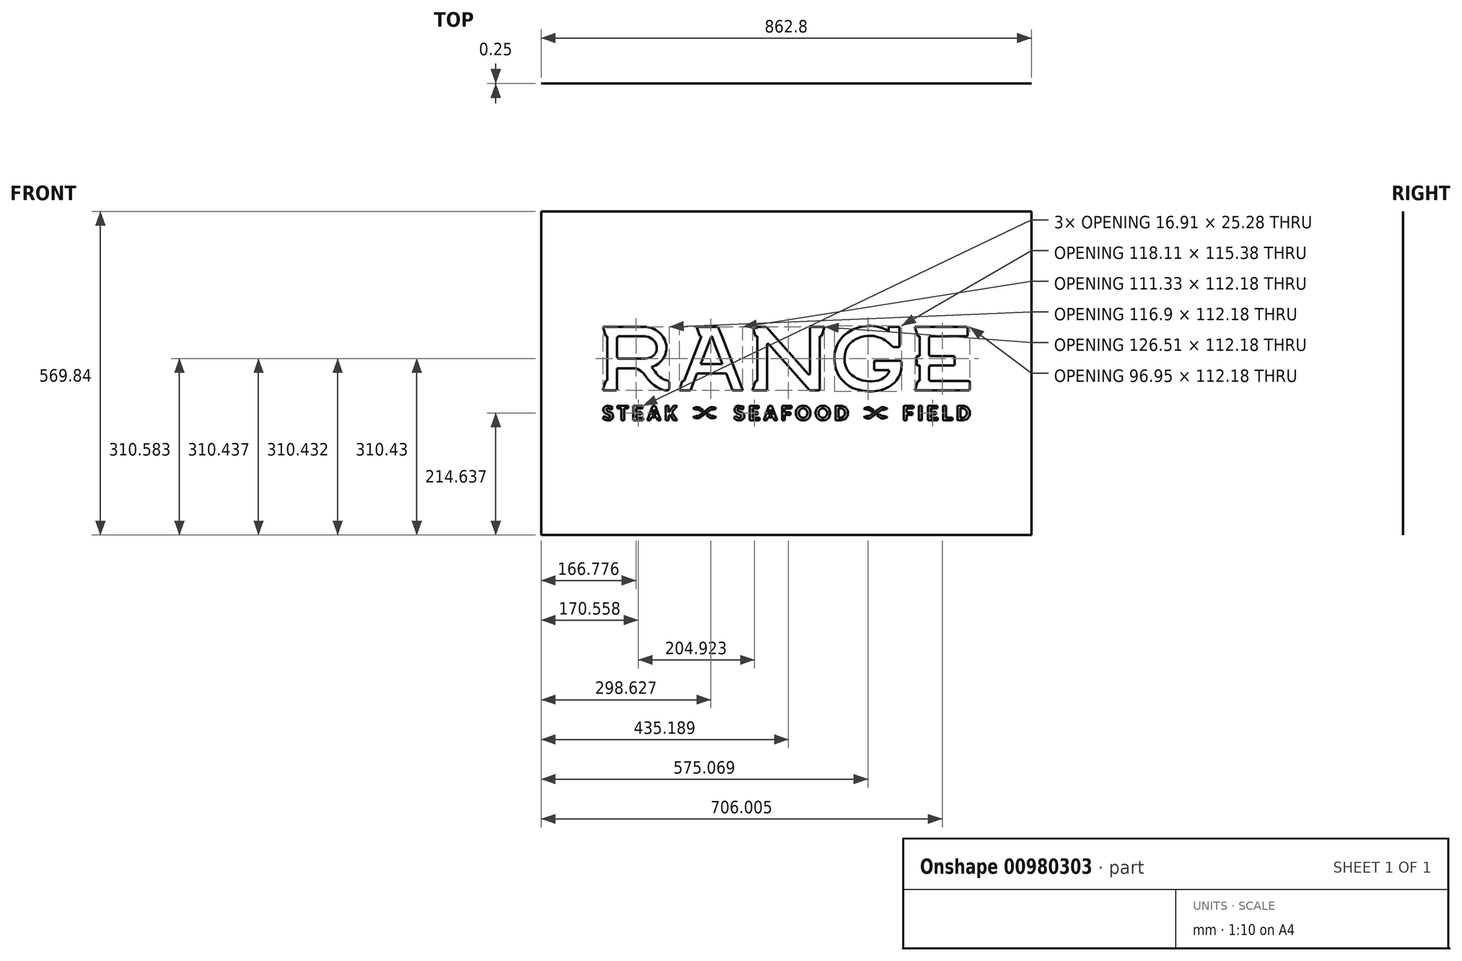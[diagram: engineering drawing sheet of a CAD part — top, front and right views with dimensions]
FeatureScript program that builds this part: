
annotation { "Feature Type Name" : "Feature", "Feature Type Description" : "" }
export const myFeature = defineFeature(function(context is Context, id is Id, definition is map)
    precondition{}
    {
        {
            var Q0;
            Q0=qCreatedBy(makeId("Front.planeOp"),FACE);
            var sketch = newSketch(context, id + "F0", { "sketchPlane" : qUnion([Q0])});
            skLineSegment(sketch, "E0", {"start": v(323.08, -28.35) * mm, "end": v(323.08, -28.56) * mm});
            skLineSegment(sketch, "E1", {"start": v(323.08, -28.56) * mm, "end": v(322.9, -29.21) * mm});
            skLineSegment(sketch, "E2", {"start": v(322.9, -29.21) * mm, "end": v(322.43, -29.93) * mm});
            skLineSegment(sketch, "E3", {"start": v(322.43, -29.93) * mm, "end": v(321.72, -30.4) * mm});
            skLineSegment(sketch, "E4", {"start": v(321.72, -30.4) * mm, "end": v(321.06, -30.58) * mm});
            skLineSegment(sketch, "E5", {"start": v(321.06, -30.58) * mm, "end": v(320.85, -30.58) * mm});
            skLineSegment(sketch, "E6", {"start": v(320.85, -30.58) * mm, "end": v(226.94, -30.58) * mm});
            skLineSegment(sketch, "E7", {"start": v(226.94, -30.58) * mm, "end": v(226.77, -30.58) * mm});
            skLineSegment(sketch, "E8", {"start": v(226.77, -30.58) * mm, "end": v(226.3, -30.29) * mm});
            skLineSegment(sketch, "E9", {"start": v(226.3, -30.29) * mm, "end": v(226.27, -30.23) * mm});
            skLineSegment(sketch, "E10", {"start": v(226.27, -30.23) * mm, "end": v(226.23, -30.18) * mm});
            skLineSegment(sketch, "E11", {"start": v(226.23, -30.18) * mm, "end": v(226.13, -29.55) * mm});
            skLineSegment(sketch, "E12", {"start": v(226.13, -29.55) * mm, "end": v(226.15, -29.49) * mm});
            skLineSegment(sketch, "E13", {"start": v(226.15, -29.49) * mm, "end": v(231.45, -13.62) * mm});
            skLineSegment(sketch, "E14", {"start": v(231.45, -13.62) * mm, "end": v(234.45, -13.62) * mm});
            skLineSegment(sketch, "E15", {"start": v(234.45, -13.62) * mm, "end": v(234.45, 13.2) * mm});
            skLineSegment(sketch, "E16", {"start": v(234.45, 13.2) * mm, "end": v(229.63, 13.2) * mm});
            skLineSegment(sketch, "E17", {"start": v(229.63, 13.2) * mm, "end": v(229.63, 30.16) * mm});
            skLineSegment(sketch, "E18", {"start": v(229.63, 30.16) * mm, "end": v(234.45, 30.16) * mm});
            skLineSegment(sketch, "E19", {"start": v(234.45, 30.16) * mm, "end": v(234.45, 64.64) * mm});
            skLineSegment(sketch, "E20", {"start": v(234.45, 64.64) * mm, "end": v(231.45, 64.64) * mm});
            skLineSegment(sketch, "E21", {"start": v(231.45, 64.64) * mm, "end": v(226.2, 80.39) * mm});
            skLineSegment(sketch, "E22", {"start": v(226.2, 80.39) * mm, "end": v(226.17, 80.46) * mm});
            skLineSegment(sketch, "E23", {"start": v(226.17, 80.46) * mm, "end": v(226.28, 81.16) * mm});
            skLineSegment(sketch, "E24", {"start": v(226.28, 81.16) * mm, "end": v(226.32, 81.22) * mm});
            skLineSegment(sketch, "E25", {"start": v(226.32, 81.22) * mm, "end": v(226.37, 81.28) * mm});
            skLineSegment(sketch, "E26", {"start": v(226.37, 81.28) * mm, "end": v(226.65, 81.5) * mm});
            skLineSegment(sketch, "E27", {"start": v(226.65, 81.5) * mm, "end": v(226.96, 81.6) * mm});
            skLineSegment(sketch, "E28", {"start": v(226.96, 81.6) * mm, "end": v(227.07, 81.6) * mm});
            skLineSegment(sketch, "E29", {"start": v(227.07, 81.6) * mm, "end": v(316.93, 81.6) * mm});
            skLineSegment(sketch, "E30", {"start": v(316.93, 81.6) * mm, "end": v(317.15, 81.6) * mm});
            skLineSegment(sketch, "E31", {"start": v(317.15, 81.6) * mm, "end": v(317.8, 81.43) * mm});
            skLineSegment(sketch, "E32", {"start": v(317.8, 81.43) * mm, "end": v(318.5, 80.95) * mm});
            skLineSegment(sketch, "E33", {"start": v(318.5, 80.95) * mm, "end": v(318.98, 80.24) * mm});
            skLineSegment(sketch, "E34", {"start": v(318.98, 80.24) * mm, "end": v(319.16, 79.59) * mm});
            skLineSegment(sketch, "E35", {"start": v(319.16, 79.59) * mm, "end": v(319.16, 79.37) * mm});
            skLineSegment(sketch, "E36", {"start": v(319.16, 79.37) * mm, "end": v(319.16, 66.87) * mm});
            skLineSegment(sketch, "E37", {"start": v(319.16, 66.87) * mm, "end": v(319.16, 66.66) * mm});
            skLineSegment(sketch, "E38", {"start": v(319.16, 66.66) * mm, "end": v(318.98, 66) * mm});
            skLineSegment(sketch, "E39", {"start": v(318.98, 66) * mm, "end": v(318.5, 65.3) * mm});
            skLineSegment(sketch, "E40", {"start": v(318.5, 65.3) * mm, "end": v(317.8, 64.82) * mm});
            skLineSegment(sketch, "E41", {"start": v(317.8, 64.82) * mm, "end": v(317.15, 64.64) * mm});
            skLineSegment(sketch, "E42", {"start": v(317.15, 64.64) * mm, "end": v(316.93, 64.64) * mm});
            skLineSegment(sketch, "E43", {"start": v(316.93, 64.64) * mm, "end": v(253.65, 64.64) * mm});
            skLineSegment(sketch, "E44", {"start": v(253.65, 64.64) * mm, "end": v(253.43, 64.64) * mm});
            skLineSegment(sketch, "E45", {"start": v(253.43, 64.64) * mm, "end": v(252.78, 64.47) * mm});
            skLineSegment(sketch, "E46", {"start": v(252.78, 64.47) * mm, "end": v(252.06, 63.98) * mm});
            skLineSegment(sketch, "E47", {"start": v(252.06, 63.98) * mm, "end": v(251.58, 63.27) * mm});
            skLineSegment(sketch, "E48", {"start": v(251.58, 63.27) * mm, "end": v(251.4, 62.61) * mm});
            skLineSegment(sketch, "E49", {"start": v(251.4, 62.61) * mm, "end": v(251.4, 62.4) * mm});
            skLineSegment(sketch, "E50", {"start": v(251.4, 62.4) * mm, "end": v(251.4, 32.4) * mm});
            skLineSegment(sketch, "E51", {"start": v(251.4, 32.4) * mm, "end": v(251.4, 32.2) * mm});
            skLineSegment(sketch, "E52", {"start": v(251.4, 32.2) * mm, "end": v(251.58, 31.54) * mm});
            skLineSegment(sketch, "E53", {"start": v(251.58, 31.54) * mm, "end": v(252.06, 30.82) * mm});
            skLineSegment(sketch, "E54", {"start": v(252.06, 30.82) * mm, "end": v(252.78, 30.34) * mm});
            skLineSegment(sketch, "E55", {"start": v(252.78, 30.34) * mm, "end": v(253.43, 30.16) * mm});
            skLineSegment(sketch, "E56", {"start": v(253.43, 30.16) * mm, "end": v(253.65, 30.16) * mm});
            skLineSegment(sketch, "E57", {"start": v(253.65, 30.16) * mm, "end": v(294.13, 30.16) * mm});
            skLineSegment(sketch, "E58", {"start": v(294.13, 30.16) * mm, "end": v(294.35, 30.16) * mm});
            skLineSegment(sketch, "E59", {"start": v(294.35, 30.16) * mm, "end": v(295, 29.99) * mm});
            skLineSegment(sketch, "E60", {"start": v(295, 29.99) * mm, "end": v(295.7, 29.51) * mm});
            skLineSegment(sketch, "E61", {"start": v(295.7, 29.51) * mm, "end": v(296.18, 28.8) * mm});
            skLineSegment(sketch, "E62", {"start": v(296.18, 28.8) * mm, "end": v(296.36, 28.15) * mm});
            skLineSegment(sketch, "E63", {"start": v(296.36, 28.15) * mm, "end": v(296.36, 27.93) * mm});
            skLineSegment(sketch, "E64", {"start": v(296.36, 27.93) * mm, "end": v(296.36, 15.43) * mm});
            skLineSegment(sketch, "E65", {"start": v(296.36, 15.43) * mm, "end": v(296.36, 15.22) * mm});
            skLineSegment(sketch, "E66", {"start": v(296.36, 15.22) * mm, "end": v(296.18, 14.57) * mm});
            skLineSegment(sketch, "E67", {"start": v(296.18, 14.57) * mm, "end": v(295.7, 13.86) * mm});
            skLineSegment(sketch, "E68", {"start": v(295.7, 13.86) * mm, "end": v(295, 13.38) * mm});
            skLineSegment(sketch, "E69", {"start": v(295, 13.38) * mm, "end": v(294.35, 13.2) * mm});
            skLineSegment(sketch, "E70", {"start": v(294.35, 13.2) * mm, "end": v(294.13, 13.2) * mm});
            skLineSegment(sketch, "E71", {"start": v(294.13, 13.2) * mm, "end": v(253.65, 13.2) * mm});
            skLineSegment(sketch, "E72", {"start": v(253.65, 13.2) * mm, "end": v(253.43, 13.2) * mm});
            skLineSegment(sketch, "E73", {"start": v(253.43, 13.2) * mm, "end": v(252.78, 13.03) * mm});
            skLineSegment(sketch, "E74", {"start": v(252.78, 13.03) * mm, "end": v(252.06, 12.55) * mm});
            skLineSegment(sketch, "E75", {"start": v(252.06, 12.55) * mm, "end": v(251.58, 11.83) * mm});
            skLineSegment(sketch, "E76", {"start": v(251.58, 11.83) * mm, "end": v(251.4, 11.17) * mm});
            skLineSegment(sketch, "E77", {"start": v(251.4, 11.17) * mm, "end": v(251.4, 10.96) * mm});
            skLineSegment(sketch, "E78", {"start": v(251.4, 10.96) * mm, "end": v(251.4, -11.37) * mm});
            skLineSegment(sketch, "E79", {"start": v(251.4, -11.37) * mm, "end": v(251.4, -11.59) * mm});
            skLineSegment(sketch, "E80", {"start": v(251.4, -11.59) * mm, "end": v(251.58, -12.25) * mm});
            skLineSegment(sketch, "E81", {"start": v(251.58, -12.25) * mm, "end": v(252.06, -12.96) * mm});
            skLineSegment(sketch, "E82", {"start": v(252.06, -12.96) * mm, "end": v(252.78, -13.44) * mm});
            skLineSegment(sketch, "E83", {"start": v(252.78, -13.44) * mm, "end": v(253.43, -13.62) * mm});
            skLineSegment(sketch, "E84", {"start": v(253.43, -13.62) * mm, "end": v(253.65, -13.62) * mm});
            skLineSegment(sketch, "E85", {"start": v(253.65, -13.62) * mm, "end": v(320.85, -13.62) * mm});
            skLineSegment(sketch, "E86", {"start": v(320.85, -13.62) * mm, "end": v(321.06, -13.62) * mm});
            skLineSegment(sketch, "E87", {"start": v(321.06, -13.62) * mm, "end": v(321.72, -13.8) * mm});
            skLineSegment(sketch, "E88", {"start": v(321.72, -13.8) * mm, "end": v(322.43, -14.27) * mm});
            skLineSegment(sketch, "E89", {"start": v(322.43, -14.27) * mm, "end": v(322.9, -14.98) * mm});
            skLineSegment(sketch, "E90", {"start": v(322.9, -14.98) * mm, "end": v(323.08, -15.63) * mm});
            skLineSegment(sketch, "E91", {"start": v(323.08, -15.63) * mm, "end": v(323.08, -15.85) * mm});
            skLineSegment(sketch, "E92", {"start": v(323.08, -15.85) * mm, "end": v(323.08, -28.35) * mm});
            skLineSegment(sketch, "E93", {"start": v(310.05, -82.92) * mm, "end": v(301.57, -82.92) * mm});
            skLineSegment(sketch, "E94", {"start": v(301.57, -82.92) * mm, "end": v(301.57, -57.64) * mm});
            skLineSegment(sketch, "E95", {"start": v(301.57, -57.64) * mm, "end": v(309.94, -57.64) * mm});
            skLineSegment(sketch, "E96", {"start": v(309.94, -57.64) * mm, "end": v(310.66, -57.64) * mm});
            skLineSegment(sketch, "E97", {"start": v(310.66, -57.64) * mm, "end": v(312.8, -57.88) * mm});
            skLineSegment(sketch, "E98", {"start": v(312.8, -57.88) * mm, "end": v(315.37, -58.57) * mm});
            skLineSegment(sketch, "E99", {"start": v(315.37, -58.57) * mm, "end": v(317.62, -59.68) * mm});
            skLineSegment(sketch, "E100", {"start": v(317.62, -59.68) * mm, "end": v(319.52, -61.18) * mm});
            skLineSegment(sketch, "E101", {"start": v(319.52, -61.18) * mm, "end": v(321.03, -63.02) * mm});
            skLineSegment(sketch, "E102", {"start": v(321.03, -63.02) * mm, "end": v(322.15, -65.18) * mm});
            skLineSegment(sketch, "E103", {"start": v(322.15, -65.18) * mm, "end": v(322.84, -67.63) * mm});
            skLineSegment(sketch, "E104", {"start": v(322.84, -67.63) * mm, "end": v(323.08, -69.64) * mm});
            skLineSegment(sketch, "E105", {"start": v(323.08, -69.64) * mm, "end": v(323.08, -70.32) * mm});
            skLineSegment(sketch, "E106", {"start": v(323.08, -70.32) * mm, "end": v(323.08, -70.99) * mm});
            skLineSegment(sketch, "E107", {"start": v(323.08, -70.99) * mm, "end": v(322.85, -73) * mm});
            skLineSegment(sketch, "E108", {"start": v(322.85, -73) * mm, "end": v(322.18, -75.43) * mm});
            skLineSegment(sketch, "E109", {"start": v(322.18, -75.43) * mm, "end": v(321.1, -77.58) * mm});
            skLineSegment(sketch, "E110", {"start": v(321.1, -77.58) * mm, "end": v(319.6, -79.41) * mm});
            skLineSegment(sketch, "E111", {"start": v(319.6, -79.41) * mm, "end": v(317.73, -80.9) * mm});
            skLineSegment(sketch, "E112", {"start": v(317.73, -80.9) * mm, "end": v(315.5, -82) * mm});
            skLineSegment(sketch, "E113", {"start": v(315.5, -82) * mm, "end": v(312.94, -82.69) * mm});
            skLineSegment(sketch, "E114", {"start": v(312.94, -82.69) * mm, "end": v(310.77, -82.92) * mm});
            skLineSegment(sketch, "E115", {"start": v(310.77, -82.92) * mm, "end": v(310.05, -82.92) * mm});
            skLineSegment(sketch, "E116", {"start": v(292.36, -82.92) * mm, "end": v(276.09, -82.92) * mm});
            skLineSegment(sketch, "E117", {"start": v(276.09, -82.92) * mm, "end": v(276.09, -57.64) * mm});
            skLineSegment(sketch, "E118", {"start": v(276.09, -57.64) * mm, "end": v(281.11, -57.64) * mm});
            skLineSegment(sketch, "E119", {"start": v(281.11, -57.64) * mm, "end": v(281.11, -78.47) * mm});
            skLineSegment(sketch, "E120", {"start": v(281.11, -78.47) * mm, "end": v(292.36, -78.47) * mm});
            skLineSegment(sketch, "E121", {"start": v(292.36, -78.47) * mm, "end": v(292.36, -82.92) * mm});
            skLineSegment(sketch, "E122", {"start": v(266.3, -82.92) * mm, "end": v(249.4, -82.92) * mm});
            skLineSegment(sketch, "E123", {"start": v(249.4, -82.92) * mm, "end": v(249.4, -57.64) * mm});
            skLineSegment(sketch, "E124", {"start": v(249.4, -57.64) * mm, "end": v(265.56, -57.64) * mm});
            skLineSegment(sketch, "E125", {"start": v(265.56, -57.64) * mm, "end": v(265.56, -62.13) * mm});
            skLineSegment(sketch, "E126", {"start": v(265.56, -62.13) * mm, "end": v(254.3, -62.13) * mm});
            skLineSegment(sketch, "E127", {"start": v(254.3, -62.13) * mm, "end": v(254.3, -68.18) * mm});
            skLineSegment(sketch, "E128", {"start": v(254.3, -68.18) * mm, "end": v(263.31, -68.18) * mm});
            skLineSegment(sketch, "E129", {"start": v(263.31, -68.18) * mm, "end": v(263.31, -72.6) * mm});
            skLineSegment(sketch, "E130", {"start": v(263.31, -72.6) * mm, "end": v(254.3, -72.6) * mm});
            skLineSegment(sketch, "E131", {"start": v(254.3, -72.6) * mm, "end": v(254.3, -78.47) * mm});
            skLineSegment(sketch, "E132", {"start": v(254.3, -78.47) * mm, "end": v(266.3, -78.47) * mm});
            skLineSegment(sketch, "E133", {"start": v(266.3, -78.47) * mm, "end": v(266.3, -82.92) * mm});
            skLineSegment(sketch, "E134", {"start": v(238.33, -82.92) * mm, "end": v(233.3, -82.92) * mm});
            skLineSegment(sketch, "E135", {"start": v(233.3, -82.92) * mm, "end": v(233.3, -57.64) * mm});
            skLineSegment(sketch, "E136", {"start": v(233.3, -57.64) * mm, "end": v(238.33, -57.64) * mm});
            skLineSegment(sketch, "E137", {"start": v(238.33, -57.64) * mm, "end": v(238.33, -82.92) * mm});
            skLineSegment(sketch, "E138", {"start": v(223.63, -62.13) * mm, "end": v(211.81, -62.13) * mm});
            skLineSegment(sketch, "E139", {"start": v(211.81, -62.13) * mm, "end": v(211.81, -68.86) * mm});
            skLineSegment(sketch, "E140", {"start": v(211.81, -68.86) * mm, "end": v(221.67, -68.86) * mm});
            skLineSegment(sketch, "E141", {"start": v(221.67, -68.86) * mm, "end": v(221.67, -73.34) * mm});
            skLineSegment(sketch, "E142", {"start": v(221.67, -73.34) * mm, "end": v(211.81, -73.34) * mm});
            skLineSegment(sketch, "E143", {"start": v(211.81, -73.34) * mm, "end": v(211.81, -82.92) * mm});
            skLineSegment(sketch, "E144", {"start": v(211.81, -82.92) * mm, "end": v(206.86, -82.92) * mm});
            skLineSegment(sketch, "E145", {"start": v(206.86, -82.92) * mm, "end": v(206.86, -57.64) * mm});
            skLineSegment(sketch, "E146", {"start": v(206.86, -57.64) * mm, "end": v(223.63, -57.64) * mm});
            skLineSegment(sketch, "E147", {"start": v(223.63, -57.64) * mm, "end": v(223.63, -62.13) * mm});
            skLineSegment(sketch, "E148", {"start": v(202.19, 7.48) * mm, "end": v(202.03, 6.34) * mm});
            skLineSegment(sketch, "E149", {"start": v(202.03, 6.34) * mm, "end": v(200.76, 0.89) * mm});
            skLineSegment(sketch, "E150", {"start": v(200.76, 0.89) * mm, "end": v(198.9, -4.25) * mm});
            skLineSegment(sketch, "E151", {"start": v(198.9, -4.25) * mm, "end": v(198.44, -5.23) * mm});
            skLineSegment(sketch, "E152", {"start": v(198.44, -5.23) * mm, "end": v(197.96, -6.24) * mm});
            skLineSegment(sketch, "E153", {"start": v(197.96, -6.24) * mm, "end": v(196.3, -9.17) * mm});
            skLineSegment(sketch, "E154", {"start": v(196.3, -9.17) * mm, "end": v(193.82, -12.77) * mm});
            skLineSegment(sketch, "E155", {"start": v(193.82, -12.77) * mm, "end": v(191.01, -16.04) * mm});
            skLineSegment(sketch, "E156", {"start": v(191.01, -16.04) * mm, "end": v(187.91, -18.99) * mm});
            skLineSegment(sketch, "E157", {"start": v(187.91, -18.99) * mm, "end": v(184.56, -21.61) * mm});
            skLineSegment(sketch, "E158", {"start": v(184.56, -21.61) * mm, "end": v(180.98, -23.93) * mm});
            skLineSegment(sketch, "E159", {"start": v(180.98, -23.93) * mm, "end": v(177.2, -25.94) * mm});
            skLineSegment(sketch, "E160", {"start": v(177.2, -25.94) * mm, "end": v(173.26, -27.66) * mm});
            skLineSegment(sketch, "E161", {"start": v(173.26, -27.66) * mm, "end": v(169.19, -29.1) * mm});
            skLineSegment(sketch, "E162", {"start": v(169.19, -29.1) * mm, "end": v(165, -30.24) * mm});
            skLineSegment(sketch, "E163", {"start": v(165, -30.24) * mm, "end": v(160.75, -31.12) * mm});
            skLineSegment(sketch, "E164", {"start": v(160.75, -31.12) * mm, "end": v(156.45, -31.73) * mm});
            skLineSegment(sketch, "E165", {"start": v(156.45, -31.73) * mm, "end": v(152.15, -32.08) * mm});
            skLineSegment(sketch, "E166", {"start": v(152.15, -32.08) * mm, "end": v(147.86, -32.17) * mm});
            skLineSegment(sketch, "E167", {"start": v(147.86, -32.17) * mm, "end": v(143.63, -32.03) * mm});
            skLineSegment(sketch, "E168", {"start": v(143.63, -32.03) * mm, "end": v(140.51, -31.77) * mm});
            skLineSegment(sketch, "E169", {"start": v(140.51, -31.77) * mm, "end": v(139.48, -31.65) * mm});
            skLineSegment(sketch, "E170", {"start": v(139.48, -31.65) * mm, "end": v(138.22, -31.5) * mm});
            skLineSegment(sketch, "E171", {"start": v(138.22, -31.5) * mm, "end": v(134.45, -30.95) * mm});
            skLineSegment(sketch, "E172", {"start": v(134.45, -30.95) * mm, "end": v(129, -29.95) * mm});
            skLineSegment(sketch, "E173", {"start": v(129, -29.95) * mm, "end": v(123.46, -28.51) * mm});
            skLineSegment(sketch, "E174", {"start": v(123.46, -28.51) * mm, "end": v(119.39, -27.1) * mm});
            skLineSegment(sketch, "E175", {"start": v(119.39, -27.1) * mm, "end": v(118.08, -26.52) * mm});
            skLineSegment(sketch, "E176", {"start": v(118.08, -26.52) * mm, "end": v(116.13, -25.66) * mm});
            skLineSegment(sketch, "E177", {"start": v(116.13, -25.66) * mm, "end": v(110.54, -22.56) * mm});
            skLineSegment(sketch, "E178", {"start": v(110.54, -22.56) * mm, "end": v(103.88, -17.76) * mm});
            skLineSegment(sketch, "E179", {"start": v(103.88, -17.76) * mm, "end": v(98.15, -12.18) * mm});
            skLineSegment(sketch, "E180", {"start": v(98.15, -12.18) * mm, "end": v(93.38, -5.89) * mm});
            skLineSegment(sketch, "E181", {"start": v(93.38, -5.89) * mm, "end": v(89.6, 1.07) * mm});
            skLineSegment(sketch, "E182", {"start": v(89.6, 1.07) * mm, "end": v(86.86, 8.63) * mm});
            skLineSegment(sketch, "E183", {"start": v(86.86, 8.63) * mm, "end": v(85.18, 16.74) * mm});
            skLineSegment(sketch, "E184", {"start": v(85.18, 16.74) * mm, "end": v(84.62, 23.19) * mm});
            skLineSegment(sketch, "E185", {"start": v(84.62, 23.19) * mm, "end": v(84.62, 25.34) * mm});
            skLineSegment(sketch, "E186", {"start": v(84.62, 25.34) * mm, "end": v(84.62, 26.9) * mm});
            skLineSegment(sketch, "E187", {"start": v(84.62, 26.9) * mm, "end": v(84.9, 31.59) * mm});
            skLineSegment(sketch, "E188", {"start": v(84.9, 31.59) * mm, "end": v(85.77, 37.59) * mm});
            skLineSegment(sketch, "E189", {"start": v(85.77, 37.59) * mm, "end": v(87.2, 43.32) * mm});
            skLineSegment(sketch, "E190", {"start": v(87.2, 43.32) * mm, "end": v(89.19, 48.76) * mm});
            skLineSegment(sketch, "E191", {"start": v(89.19, 48.76) * mm, "end": v(91.73, 53.9) * mm});
            skLineSegment(sketch, "E192", {"start": v(91.73, 53.9) * mm, "end": v(94.8, 58.72) * mm});
            skLineSegment(sketch, "E193", {"start": v(94.8, 58.72) * mm, "end": v(98.41, 63.19) * mm});
            skLineSegment(sketch, "E194", {"start": v(98.41, 63.19) * mm, "end": v(101.46, 66.33) * mm});
            skLineSegment(sketch, "E195", {"start": v(101.46, 66.33) * mm, "end": v(102.55, 67.3) * mm});
            skLineSegment(sketch, "E196", {"start": v(102.55, 67.3) * mm, "end": v(103.62, 68.26) * mm});
            skLineSegment(sketch, "E197", {"start": v(103.62, 68.26) * mm, "end": v(107.04, 70.91) * mm});
            skLineSegment(sketch, "E198", {"start": v(107.04, 70.91) * mm, "end": v(111.94, 74.09) * mm});
            skLineSegment(sketch, "E199", {"start": v(111.94, 74.09) * mm, "end": v(117.18, 76.81) * mm});
            skLineSegment(sketch, "E200", {"start": v(117.18, 76.81) * mm, "end": v(122.73, 79.08) * mm});
            skLineSegment(sketch, "E201", {"start": v(122.73, 79.08) * mm, "end": v(128.53, 80.86) * mm});
            skLineSegment(sketch, "E202", {"start": v(128.53, 80.86) * mm, "end": v(134.54, 82.16) * mm});
            skLineSegment(sketch, "E203", {"start": v(134.54, 82.16) * mm, "end": v(140.7, 82.94) * mm});
            skLineSegment(sketch, "E204", {"start": v(140.7, 82.94) * mm, "end": v(145.41, 83.2) * mm});
            skLineSegment(sketch, "E205", {"start": v(145.41, 83.2) * mm, "end": v(146.98, 83.2) * mm});
            skLineSegment(sketch, "E206", {"start": v(146.98, 83.2) * mm, "end": v(148.81, 83.2) * mm});
            skLineSegment(sketch, "E207", {"start": v(148.81, 83.2) * mm, "end": v(153.71, 82.9) * mm});
            skLineSegment(sketch, "E208", {"start": v(153.71, 82.9) * mm, "end": v(154.32, 82.85) * mm});
            skLineSegment(sketch, "E209", {"start": v(154.32, 82.85) * mm, "end": v(156.23, 82.66) * mm});
            skLineSegment(sketch, "E210", {"start": v(156.23, 82.66) * mm, "end": v(161.9, 81.58) * mm});
            skLineSegment(sketch, "E211", {"start": v(161.9, 81.58) * mm, "end": v(168.6, 79.56) * mm});
            skLineSegment(sketch, "E212", {"start": v(168.6, 79.56) * mm, "end": v(174.42, 77.11) * mm});
            skLineSegment(sketch, "E213", {"start": v(174.42, 77.11) * mm, "end": v(178.17, 75.24) * mm});
            skLineSegment(sketch, "E214", {"start": v(178.17, 75.24) * mm, "end": v(179.4, 74.57) * mm});
            skLineSegment(sketch, "E215", {"start": v(179.4, 74.57) * mm, "end": v(180.37, 74.04) * mm});
            skLineSegment(sketch, "E216", {"start": v(180.37, 74.04) * mm, "end": v(180.37, 81.6) * mm});
            skLineSegment(sketch, "E217", {"start": v(180.37, 81.6) * mm, "end": v(198.26, 81.6) * mm});
            skLineSegment(sketch, "E218", {"start": v(198.26, 81.6) * mm, "end": v(198.38, 81.6) * mm});
            skLineSegment(sketch, "E219", {"start": v(198.38, 81.6) * mm, "end": v(198.75, 81.4) * mm});
            skLineSegment(sketch, "E220", {"start": v(198.75, 81.4) * mm, "end": v(198.95, 81.05) * mm});
            skLineSegment(sketch, "E221", {"start": v(198.95, 81.05) * mm, "end": v(198.95, 80.92) * mm});
            skLineSegment(sketch, "E222", {"start": v(198.95, 80.92) * mm, "end": v(198.95, 46.7) * mm});
            skLineSegment(sketch, "E223", {"start": v(198.95, 46.7) * mm, "end": v(198.95, 46.59) * mm});
            skLineSegment(sketch, "E224", {"start": v(198.95, 46.59) * mm, "end": v(198.75, 46.23) * mm});
            skLineSegment(sketch, "E225", {"start": v(198.75, 46.23) * mm, "end": v(198.38, 46.03) * mm});
            skLineSegment(sketch, "E226", {"start": v(198.38, 46.03) * mm, "end": v(198.26, 46.03) * mm});
            skLineSegment(sketch, "E227", {"start": v(198.26, 46.03) * mm, "end": v(188.6, 46.03) * mm});
            skLineSegment(sketch, "E228", {"start": v(188.6, 46.03) * mm, "end": v(187.91, 46.28) * mm});
            skLineSegment(sketch, "E229", {"start": v(187.91, 46.28) * mm, "end": v(182.92, 50.61) * mm});
            skLineSegment(sketch, "E230", {"start": v(182.92, 50.61) * mm, "end": v(182.91, 50.62) * mm});
            skLineSegment(sketch, "E231", {"start": v(182.91, 50.62) * mm, "end": v(182.8, 50.71) * mm});
            skLineSegment(sketch, "E232", {"start": v(182.8, 50.71) * mm, "end": v(182.5, 50.97) * mm});
            skLineSegment(sketch, "E233", {"start": v(182.5, 50.97) * mm, "end": v(182.1, 51.33) * mm});
            skLineSegment(sketch, "E234", {"start": v(182.1, 51.33) * mm, "end": v(181.63, 51.74) * mm});
            skLineSegment(sketch, "E235", {"start": v(181.63, 51.74) * mm, "end": v(181.16, 52.14) * mm});
            skLineSegment(sketch, "E236", {"start": v(181.16, 52.14) * mm, "end": v(180.75, 52.5) * mm});
            skLineSegment(sketch, "E237", {"start": v(180.75, 52.5) * mm, "end": v(180.47, 52.75) * mm});
            skLineSegment(sketch, "E238", {"start": v(180.47, 52.75) * mm, "end": v(180.36, 52.84) * mm});
            skLineSegment(sketch, "E239", {"start": v(180.36, 52.84) * mm, "end": v(179.96, 53.16) * mm});
            skLineSegment(sketch, "E240", {"start": v(179.96, 53.16) * mm, "end": v(178.76, 54.12) * mm});
            skLineSegment(sketch, "E241", {"start": v(178.76, 54.12) * mm, "end": v(176.55, 55.78) * mm});
            skLineSegment(sketch, "E242", {"start": v(176.55, 55.78) * mm, "end": v(173.75, 57.67) * mm});
            skLineSegment(sketch, "E243", {"start": v(173.75, 57.67) * mm, "end": v(170.43, 59.65) * mm});
            skLineSegment(sketch, "E244", {"start": v(170.43, 59.65) * mm, "end": v(166.61, 61.56) * mm});
            skLineSegment(sketch, "E245", {"start": v(166.61, 61.56) * mm, "end": v(162.34, 63.26) * mm});
            skLineSegment(sketch, "E246", {"start": v(162.34, 63.26) * mm, "end": v(157.64, 64.59) * mm});
            skLineSegment(sketch, "E247", {"start": v(157.64, 64.59) * mm, "end": v(153.84, 65.28) * mm});
            skLineSegment(sketch, "E248", {"start": v(153.84, 65.28) * mm, "end": v(152.57, 65.4) * mm});
            skLineSegment(sketch, "E249", {"start": v(152.57, 65.4) * mm, "end": v(151.22, 65.54) * mm});
            skLineSegment(sketch, "E250", {"start": v(151.22, 65.54) * mm, "end": v(147.16, 65.69) * mm});
            skLineSegment(sketch, "E251", {"start": v(147.16, 65.69) * mm, "end": v(141.84, 65.46) * mm});
            skLineSegment(sketch, "E252", {"start": v(141.84, 65.46) * mm, "end": v(136.63, 64.75) * mm});
            skLineSegment(sketch, "E253", {"start": v(136.63, 64.75) * mm, "end": v(131.62, 63.55) * mm});
            skLineSegment(sketch, "E254", {"start": v(131.62, 63.55) * mm, "end": v(126.85, 61.9) * mm});
            skLineSegment(sketch, "E255", {"start": v(126.85, 61.9) * mm, "end": v(122.36, 59.8) * mm});
            skLineSegment(sketch, "E256", {"start": v(122.36, 59.8) * mm, "end": v(118.22, 57.27) * mm});
            skLineSegment(sketch, "E257", {"start": v(118.22, 57.27) * mm, "end": v(115.37, 55.11) * mm});
            skLineSegment(sketch, "E258", {"start": v(115.37, 55.11) * mm, "end": v(114.49, 54.32) * mm});
            skLineSegment(sketch, "E259", {"start": v(114.49, 54.32) * mm, "end": v(113.03, 53.02) * mm});
            skLineSegment(sketch, "E260", {"start": v(113.03, 53.02) * mm, "end": v(109.22, 48.46) * mm});
            skLineSegment(sketch, "E261", {"start": v(109.22, 48.46) * mm, "end": v(105.44, 41.67) * mm});
            skLineSegment(sketch, "E262", {"start": v(105.44, 41.67) * mm, "end": v(103.16, 33.96) * mm});
            skLineSegment(sketch, "E263", {"start": v(103.16, 33.96) * mm, "end": v(102.4, 27.51) * mm});
            skLineSegment(sketch, "E264", {"start": v(102.4, 27.51) * mm, "end": v(102.4, 25.36) * mm});
            skLineSegment(sketch, "E265", {"start": v(102.4, 25.36) * mm, "end": v(102.4, 23.87) * mm});
            skLineSegment(sketch, "E266", {"start": v(102.4, 23.87) * mm, "end": v(102.77, 19.41) * mm});
            skLineSegment(sketch, "E267", {"start": v(102.77, 19.41) * mm, "end": v(103.87, 13.9) * mm});
            skLineSegment(sketch, "E268", {"start": v(103.87, 13.9) * mm, "end": v(105.7, 8.84) * mm});
            skLineSegment(sketch, "E269", {"start": v(105.7, 8.84) * mm, "end": v(108.27, 4.22) * mm});
            skLineSegment(sketch, "E270", {"start": v(108.27, 4.22) * mm, "end": v(111.56, 0.04) * mm});
            skLineSegment(sketch, "E271", {"start": v(111.56, 0.04) * mm, "end": v(115.57, -3.68) * mm});
            skLineSegment(sketch, "E272", {"start": v(115.57, -3.68) * mm, "end": v(120.31, -6.95) * mm});
            skLineSegment(sketch, "E273", {"start": v(120.31, -6.95) * mm, "end": v(124.36, -9.14) * mm});
            skLineSegment(sketch, "E274", {"start": v(124.36, -9.14) * mm, "end": v(125.76, -9.76) * mm});
            skLineSegment(sketch, "E275", {"start": v(125.76, -9.76) * mm, "end": v(126.95, -10.29) * mm});
            skLineSegment(sketch, "E276", {"start": v(126.95, -10.29) * mm, "end": v(130.63, -11.61) * mm});
            skLineSegment(sketch, "E277", {"start": v(130.63, -11.61) * mm, "end": v(135.74, -13.01) * mm});
            skLineSegment(sketch, "E278", {"start": v(135.74, -13.01) * mm, "end": v(141.01, -13.95) * mm});
            skLineSegment(sketch, "E279", {"start": v(141.01, -13.95) * mm, "end": v(146.31, -14.42) * mm});
            skLineSegment(sketch, "E280", {"start": v(146.31, -14.42) * mm, "end": v(151.54, -14.43) * mm});
            skLineSegment(sketch, "E281", {"start": v(151.54, -14.43) * mm, "end": v(156.6, -13.95) * mm});
            skLineSegment(sketch, "E282", {"start": v(156.6, -13.95) * mm, "end": v(161.36, -13) * mm});
            skLineSegment(sketch, "E283", {"start": v(161.36, -13) * mm, "end": v(164.66, -12) * mm});
            skLineSegment(sketch, "E284", {"start": v(164.66, -12) * mm, "end": v(165.72, -11.56) * mm});
            skLineSegment(sketch, "E285", {"start": v(165.72, -11.56) * mm, "end": v(166.78, -11.13) * mm});
            skLineSegment(sketch, "E286", {"start": v(166.78, -11.13) * mm, "end": v(171.68, -8.31) * mm});
            skLineSegment(sketch, "E287", {"start": v(171.68, -8.31) * mm, "end": v(175.87, -4.72) * mm});
            skLineSegment(sketch, "E288", {"start": v(175.87, -4.72) * mm, "end": v(176.58, -3.9) * mm});
            skLineSegment(sketch, "E289", {"start": v(176.58, -3.9) * mm, "end": v(176.6, -3.89) * mm});
            skLineSegment(sketch, "E290", {"start": v(176.6, -3.89) * mm, "end": v(176.82, -3.62) * mm});
            skLineSegment(sketch, "E291", {"start": v(176.82, -3.62) * mm, "end": v(177.4, -2.88) * mm});
            skLineSegment(sketch, "E292", {"start": v(177.4, -2.88) * mm, "end": v(178.19, -1.81) * mm});
            skLineSegment(sketch, "E293", {"start": v(178.19, -1.81) * mm, "end": v(179.06, -0.52) * mm});
            skLineSegment(sketch, "E294", {"start": v(179.06, -0.52) * mm, "end": v(179.88, 0.88) * mm});
            skLineSegment(sketch, "E295", {"start": v(179.88, 0.88) * mm, "end": v(180.5, 2.28) * mm});
            skLineSegment(sketch, "E296", {"start": v(180.5, 2.28) * mm, "end": v(180.83, 3.55) * mm});
            skLineSegment(sketch, "E297", {"start": v(180.83, 3.55) * mm, "end": v(180.8, 4.37) * mm});
            skLineSegment(sketch, "E298", {"start": v(180.8, 4.37) * mm, "end": v(180.69, 4.6) * mm});
            skLineSegment(sketch, "E299", {"start": v(180.69, 4.6) * mm, "end": v(180.65, 4.7) * mm});
            skLineSegment(sketch, "E300", {"start": v(180.65, 4.7) * mm, "end": v(180.48, 4.93) * mm});
            skLineSegment(sketch, "E301", {"start": v(180.48, 4.93) * mm, "end": v(180.15, 5.23) * mm});
            skLineSegment(sketch, "E302", {"start": v(180.15, 5.23) * mm, "end": v(179.65, 5.46) * mm});
            skLineSegment(sketch, "E303", {"start": v(179.65, 5.46) * mm, "end": v(179.12, 5.55) * mm});
            skLineSegment(sketch, "E304", {"start": v(179.12, 5.55) * mm, "end": v(178.95, 5.55) * mm});
            skLineSegment(sketch, "E305", {"start": v(178.95, 5.55) * mm, "end": v(155.69, 5.55) * mm});
            skLineSegment(sketch, "E306", {"start": v(155.69, 5.55) * mm, "end": v(155.57, 5.55) * mm});
            skLineSegment(sketch, "E307", {"start": v(155.57, 5.55) * mm, "end": v(155.2, 5.74) * mm});
            skLineSegment(sketch, "E308", {"start": v(155.2, 5.74) * mm, "end": v(155, 6.1) * mm});
            skLineSegment(sketch, "E309", {"start": v(155, 6.1) * mm, "end": v(155, 6.22) * mm});
            skLineSegment(sketch, "E310", {"start": v(155, 6.22) * mm, "end": v(155, 21.31) * mm});
            skLineSegment(sketch, "E311", {"start": v(155, 21.31) * mm, "end": v(155, 21.43) * mm});
            skLineSegment(sketch, "E312", {"start": v(155, 21.43) * mm, "end": v(155.2, 21.8) * mm});
            skLineSegment(sketch, "E313", {"start": v(155.2, 21.8) * mm, "end": v(155.57, 22) * mm});
            skLineSegment(sketch, "E314", {"start": v(155.57, 22) * mm, "end": v(155.69, 22) * mm});
            skLineSegment(sketch, "E315", {"start": v(155.69, 22) * mm, "end": v(200.36, 22) * mm});
            skLineSegment(sketch, "E316", {"start": v(200.36, 22) * mm, "end": v(200.58, 22) * mm});
            skLineSegment(sketch, "E317", {"start": v(200.58, 22) * mm, "end": v(201.27, 21.81) * mm});
            skLineSegment(sketch, "E318", {"start": v(201.27, 21.81) * mm, "end": v(202.02, 21.32) * mm});
            skLineSegment(sketch, "E319", {"start": v(202.02, 21.32) * mm, "end": v(202.53, 20.6) * mm});
            skLineSegment(sketch, "E320", {"start": v(202.53, 20.6) * mm, "end": v(202.72, 19.92) * mm});
            skLineSegment(sketch, "E321", {"start": v(202.72, 19.92) * mm, "end": v(202.72, 19.7) * mm});
            skLineSegment(sketch, "E322", {"start": v(202.72, 19.7) * mm, "end": v(202.72, 18.75) * mm});
            skLineSegment(sketch, "E323", {"start": v(202.72, 18.75) * mm, "end": v(202.68, 13.7) * mm});
            skLineSegment(sketch, "E324", {"start": v(202.68, 13.7) * mm, "end": v(202.33, 8.5) * mm});
            skLineSegment(sketch, "E325", {"start": v(202.33, 8.5) * mm, "end": v(202.19, 7.48) * mm});
            skLineSegment(sketch, "E326", {"start": v(136.23, -62.31) * mm, "end": v(136.66, -62.13) * mm});
            skLineSegment(sketch, "E327", {"start": v(136.66, -62.13) * mm, "end": v(140.92, -60.65) * mm});
            skLineSegment(sketch, "E328", {"start": v(140.92, -60.65) * mm, "end": v(141.35, -60.52) * mm});
            skLineSegment(sketch, "E329", {"start": v(141.35, -60.52) * mm, "end": v(141.57, -60.42) * mm});
            skLineSegment(sketch, "E330", {"start": v(141.57, -60.42) * mm, "end": v(142.63, -60.3) * mm});
            skLineSegment(sketch, "E331", {"start": v(142.63, -60.3) * mm, "end": v(143.7, -60.35) * mm});
            skLineSegment(sketch, "E332", {"start": v(143.7, -60.35) * mm, "end": v(143.9, -60.33) * mm});
            skLineSegment(sketch, "E333", {"start": v(143.9, -60.33) * mm, "end": v(147.11, -60.33) * mm});
            skLineSegment(sketch, "E334", {"start": v(147.11, -60.33) * mm, "end": v(147.63, -60.7) * mm});
            skLineSegment(sketch, "E335", {"start": v(147.63, -60.7) * mm, "end": v(154.06, -65.38) * mm});
            skLineSegment(sketch, "E336", {"start": v(154.06, -65.38) * mm, "end": v(150.69, -67.82) * mm});
            skLineSegment(sketch, "E337", {"start": v(150.69, -67.82) * mm, "end": v(145.83, -64.3) * mm});
            skLineSegment(sketch, "E338", {"start": v(145.83, -64.3) * mm, "end": v(143.9, -64.3) * mm});
            skLineSegment(sketch, "E339", {"start": v(143.9, -64.3) * mm, "end": v(143.7, -64.27) * mm});
            skLineSegment(sketch, "E340", {"start": v(143.7, -64.27) * mm, "end": v(142.63, -64.32) * mm});
            skLineSegment(sketch, "E341", {"start": v(142.63, -64.32) * mm, "end": v(141.57, -64.2) * mm});
            skLineSegment(sketch, "E342", {"start": v(141.57, -64.2) * mm, "end": v(141.35, -64.1) * mm});
            skLineSegment(sketch, "E343", {"start": v(141.35, -64.1) * mm, "end": v(140.92, -63.97) * mm});
            skLineSegment(sketch, "E344", {"start": v(140.92, -63.97) * mm, "end": v(136.66, -62.49) * mm});
            skLineSegment(sketch, "E345", {"start": v(136.66, -62.49) * mm, "end": v(136.23, -62.31) * mm});
            skLineSegment(sketch, "E346", {"start": v(172.66, -64.07) * mm, "end": v(172.45, -64.18) * mm});
            skLineSegment(sketch, "E347", {"start": v(172.45, -64.18) * mm, "end": v(171.38, -64.32) * mm});
            skLineSegment(sketch, "E348", {"start": v(171.38, -64.32) * mm, "end": v(170.32, -64.28) * mm});
            skLineSegment(sketch, "E349", {"start": v(170.32, -64.28) * mm, "end": v(170.1, -64.3) * mm});
            skLineSegment(sketch, "E350", {"start": v(170.1, -64.3) * mm, "end": v(168.19, -64.3) * mm});
            skLineSegment(sketch, "E351", {"start": v(168.19, -64.3) * mm, "end": v(147.63, -79.22) * mm});
            skLineSegment(sketch, "E352", {"start": v(147.63, -79.22) * mm, "end": v(147.11, -79.6) * mm});
            skLineSegment(sketch, "E353", {"start": v(147.11, -79.6) * mm, "end": v(143.9, -79.6) * mm});
            skLineSegment(sketch, "E354", {"start": v(143.9, -79.6) * mm, "end": v(143.7, -79.58) * mm});
            skLineSegment(sketch, "E355", {"start": v(143.7, -79.58) * mm, "end": v(142.63, -79.63) * mm});
            skLineSegment(sketch, "E356", {"start": v(142.63, -79.63) * mm, "end": v(141.57, -79.51) * mm});
            skLineSegment(sketch, "E357", {"start": v(141.57, -79.51) * mm, "end": v(141.35, -79.41) * mm});
            skLineSegment(sketch, "E358", {"start": v(141.35, -79.41) * mm, "end": v(140.92, -79.28) * mm});
            skLineSegment(sketch, "E359", {"start": v(140.92, -79.28) * mm, "end": v(136.66, -77.8) * mm});
            skLineSegment(sketch, "E360", {"start": v(136.66, -77.8) * mm, "end": v(136.23, -77.62) * mm});
            skLineSegment(sketch, "E361", {"start": v(136.23, -77.62) * mm, "end": v(136.66, -77.44) * mm});
            skLineSegment(sketch, "E362", {"start": v(136.66, -77.44) * mm, "end": v(140.92, -75.96) * mm});
            skLineSegment(sketch, "E363", {"start": v(140.92, -75.96) * mm, "end": v(141.35, -75.83) * mm});
            skLineSegment(sketch, "E364", {"start": v(141.35, -75.83) * mm, "end": v(141.57, -75.73) * mm});
            skLineSegment(sketch, "E365", {"start": v(141.57, -75.73) * mm, "end": v(142.63, -75.6) * mm});
            skLineSegment(sketch, "E366", {"start": v(142.63, -75.6) * mm, "end": v(143.7, -75.66) * mm});
            skLineSegment(sketch, "E367", {"start": v(143.7, -75.66) * mm, "end": v(143.9, -75.64) * mm});
            skLineSegment(sketch, "E368", {"start": v(143.9, -75.64) * mm, "end": v(145.83, -75.64) * mm});
            skLineSegment(sketch, "E369", {"start": v(145.83, -75.64) * mm, "end": v(166.38, -60.7) * mm});
            skLineSegment(sketch, "E370", {"start": v(166.38, -60.7) * mm, "end": v(166.9, -60.33) * mm});
            skLineSegment(sketch, "E371", {"start": v(166.9, -60.33) * mm, "end": v(170.1, -60.33) * mm});
            skLineSegment(sketch, "E372", {"start": v(170.1, -60.33) * mm, "end": v(170.32, -60.34) * mm});
            skLineSegment(sketch, "E373", {"start": v(170.32, -60.34) * mm, "end": v(171.38, -60.3) * mm});
            skLineSegment(sketch, "E374", {"start": v(171.38, -60.3) * mm, "end": v(172.45, -60.44) * mm});
            skLineSegment(sketch, "E375", {"start": v(172.45, -60.44) * mm, "end": v(172.66, -60.55) * mm});
            skLineSegment(sketch, "E376", {"start": v(172.66, -60.55) * mm, "end": v(173.09, -60.68) * mm});
            skLineSegment(sketch, "E377", {"start": v(173.09, -60.68) * mm, "end": v(177.35, -62.14) * mm});
            skLineSegment(sketch, "E378", {"start": v(177.35, -62.14) * mm, "end": v(177.78, -62.31) * mm});
            skLineSegment(sketch, "E379", {"start": v(177.78, -62.31) * mm, "end": v(177.35, -62.48) * mm});
            skLineSegment(sketch, "E380", {"start": v(177.35, -62.48) * mm, "end": v(173.09, -63.94) * mm});
            skLineSegment(sketch, "E381", {"start": v(173.09, -63.94) * mm, "end": v(172.66, -64.07) * mm});
            skLineSegment(sketch, "E382", {"start": v(172.66, -79.38) * mm, "end": v(172.45, -79.49) * mm});
            skLineSegment(sketch, "E383", {"start": v(172.45, -79.49) * mm, "end": v(171.38, -79.63) * mm});
            skLineSegment(sketch, "E384", {"start": v(171.38, -79.63) * mm, "end": v(170.32, -79.59) * mm});
            skLineSegment(sketch, "E385", {"start": v(170.32, -79.59) * mm, "end": v(170.1, -79.6) * mm});
            skLineSegment(sketch, "E386", {"start": v(170.1, -79.6) * mm, "end": v(166.9, -79.6) * mm});
            skLineSegment(sketch, "E387", {"start": v(166.9, -79.6) * mm, "end": v(166.38, -79.22) * mm});
            skLineSegment(sketch, "E388", {"start": v(166.38, -79.22) * mm, "end": v(159.96, -74.56) * mm});
            skLineSegment(sketch, "E389", {"start": v(159.96, -74.56) * mm, "end": v(163.33, -72.11) * mm});
            skLineSegment(sketch, "E390", {"start": v(163.33, -72.11) * mm, "end": v(168.19, -75.64) * mm});
            skLineSegment(sketch, "E391", {"start": v(168.19, -75.64) * mm, "end": v(170.1, -75.64) * mm});
            skLineSegment(sketch, "E392", {"start": v(170.1, -75.64) * mm, "end": v(170.32, -75.65) * mm});
            skLineSegment(sketch, "E393", {"start": v(170.32, -75.65) * mm, "end": v(171.38, -75.62) * mm});
            skLineSegment(sketch, "E394", {"start": v(171.38, -75.62) * mm, "end": v(172.45, -75.76) * mm});
            skLineSegment(sketch, "E395", {"start": v(172.45, -75.76) * mm, "end": v(172.66, -75.86) * mm});
            skLineSegment(sketch, "E396", {"start": v(172.66, -75.86) * mm, "end": v(173.09, -75.99) * mm});
            skLineSegment(sketch, "E397", {"start": v(173.09, -75.99) * mm, "end": v(177.35, -77.45) * mm});
            skLineSegment(sketch, "E398", {"start": v(177.35, -77.45) * mm, "end": v(177.78, -77.62) * mm});
            skLineSegment(sketch, "E399", {"start": v(177.78, -77.62) * mm, "end": v(177.35, -77.8) * mm});
            skLineSegment(sketch, "E400", {"start": v(177.35, -77.8) * mm, "end": v(173.09, -79.25) * mm});
            skLineSegment(sketch, "E401", {"start": v(173.09, -79.25) * mm, "end": v(172.66, -79.38) * mm});
            skLineSegment(sketch, "E402", {"start": v(95.44, -82.92) * mm, "end": v(86.97, -82.92) * mm});
            skLineSegment(sketch, "E403", {"start": v(86.97, -82.92) * mm, "end": v(86.97, -57.64) * mm});
            skLineSegment(sketch, "E404", {"start": v(86.97, -57.64) * mm, "end": v(95.33, -57.64) * mm});
            skLineSegment(sketch, "E405", {"start": v(95.33, -57.64) * mm, "end": v(96.05, -57.64) * mm});
            skLineSegment(sketch, "E406", {"start": v(96.05, -57.64) * mm, "end": v(98.2, -57.88) * mm});
            skLineSegment(sketch, "E407", {"start": v(98.2, -57.88) * mm, "end": v(100.76, -58.57) * mm});
            skLineSegment(sketch, "E408", {"start": v(100.76, -58.57) * mm, "end": v(103.01, -59.68) * mm});
            skLineSegment(sketch, "E409", {"start": v(103.01, -59.68) * mm, "end": v(104.9, -61.18) * mm});
            skLineSegment(sketch, "E410", {"start": v(104.9, -61.18) * mm, "end": v(106.42, -63.02) * mm});
            skLineSegment(sketch, "E411", {"start": v(106.42, -63.02) * mm, "end": v(107.54, -65.18) * mm});
            skLineSegment(sketch, "E412", {"start": v(107.54, -65.18) * mm, "end": v(108.24, -67.63) * mm});
            skLineSegment(sketch, "E413", {"start": v(108.24, -67.63) * mm, "end": v(108.47, -69.64) * mm});
            skLineSegment(sketch, "E414", {"start": v(108.47, -69.64) * mm, "end": v(108.47, -70.32) * mm});
            skLineSegment(sketch, "E415", {"start": v(108.47, -70.32) * mm, "end": v(108.47, -70.99) * mm});
            skLineSegment(sketch, "E416", {"start": v(108.47, -70.99) * mm, "end": v(108.24, -73) * mm});
            skLineSegment(sketch, "E417", {"start": v(108.24, -73) * mm, "end": v(107.57, -75.43) * mm});
            skLineSegment(sketch, "E418", {"start": v(107.57, -75.43) * mm, "end": v(106.49, -77.58) * mm});
            skLineSegment(sketch, "E419", {"start": v(106.49, -77.58) * mm, "end": v(105, -79.41) * mm});
            skLineSegment(sketch, "E420", {"start": v(105, -79.41) * mm, "end": v(103.13, -80.9) * mm});
            skLineSegment(sketch, "E421", {"start": v(103.13, -80.9) * mm, "end": v(100.9, -82) * mm});
            skLineSegment(sketch, "E422", {"start": v(100.9, -82) * mm, "end": v(98.33, -82.69) * mm});
            skLineSegment(sketch, "E423", {"start": v(98.33, -82.69) * mm, "end": v(96.16, -82.92) * mm});
            skLineSegment(sketch, "E424", {"start": v(96.16, -82.92) * mm, "end": v(95.44, -82.92) * mm});
            skLineSegment(sketch, "E425", {"start": v(64.26, -83.2) * mm, "end": v(63.57, -83.2) * mm});
            skLineSegment(sketch, "E426", {"start": v(63.57, -83.2) * mm, "end": v(61.5, -82.96) * mm});
            skLineSegment(sketch, "E427", {"start": v(61.5, -82.96) * mm, "end": v(59.02, -82.24) * mm});
            skLineSegment(sketch, "E428", {"start": v(59.02, -82.24) * mm, "end": v(56.82, -81.09) * mm});
            skLineSegment(sketch, "E429", {"start": v(56.82, -81.09) * mm, "end": v(54.94, -79.55) * mm});
            skLineSegment(sketch, "E430", {"start": v(54.94, -79.55) * mm, "end": v(53.43, -77.66) * mm});
            skLineSegment(sketch, "E431", {"start": v(53.43, -77.66) * mm, "end": v(52.3, -75.46) * mm});
            skLineSegment(sketch, "E432", {"start": v(52.3, -75.46) * mm, "end": v(51.6, -72.99) * mm});
            skLineSegment(sketch, "E433", {"start": v(51.6, -72.99) * mm, "end": v(51.37, -70.96) * mm});
            skLineSegment(sketch, "E434", {"start": v(51.37, -70.96) * mm, "end": v(51.37, -70.28) * mm});
            skLineSegment(sketch, "E435", {"start": v(51.37, -70.28) * mm, "end": v(51.37, -69.6) * mm});
            skLineSegment(sketch, "E436", {"start": v(51.37, -69.6) * mm, "end": v(51.6, -67.57) * mm});
            skLineSegment(sketch, "E437", {"start": v(51.6, -67.57) * mm, "end": v(52.3, -65.09) * mm});
            skLineSegment(sketch, "E438", {"start": v(52.3, -65.09) * mm, "end": v(53.43, -62.88) * mm});
            skLineSegment(sketch, "E439", {"start": v(53.43, -62.88) * mm, "end": v(54.94, -60.98) * mm});
            skLineSegment(sketch, "E440", {"start": v(54.94, -60.98) * mm, "end": v(56.82, -59.44) * mm});
            skLineSegment(sketch, "E441", {"start": v(56.82, -59.44) * mm, "end": v(59.02, -58.29) * mm});
            skLineSegment(sketch, "E442", {"start": v(59.02, -58.29) * mm, "end": v(61.5, -57.57) * mm});
            skLineSegment(sketch, "E443", {"start": v(61.5, -57.57) * mm, "end": v(63.57, -57.32) * mm});
            skLineSegment(sketch, "E444", {"start": v(63.57, -57.32) * mm, "end": v(64.26, -57.32) * mm});
            skLineSegment(sketch, "E445", {"start": v(64.26, -57.32) * mm, "end": v(64.93, -57.32) * mm});
            skLineSegment(sketch, "E446", {"start": v(64.93, -57.32) * mm, "end": v(66.94, -57.56) * mm});
            skLineSegment(sketch, "E447", {"start": v(66.94, -57.56) * mm, "end": v(69.4, -58.26) * mm});
            skLineSegment(sketch, "E448", {"start": v(69.4, -58.26) * mm, "end": v(71.6, -59.38) * mm});
            skLineSegment(sketch, "E449", {"start": v(71.6, -59.38) * mm, "end": v(73.48, -60.9) * mm});
            skLineSegment(sketch, "E450", {"start": v(73.48, -60.9) * mm, "end": v(75, -62.78) * mm});
            skLineSegment(sketch, "E451", {"start": v(75, -62.78) * mm, "end": v(76.15, -65) * mm});
            skLineSegment(sketch, "E452", {"start": v(76.15, -65) * mm, "end": v(76.87, -67.5) * mm});
            skLineSegment(sketch, "E453", {"start": v(76.87, -67.5) * mm, "end": v(77.12, -69.59) * mm});
            skLineSegment(sketch, "E454", {"start": v(77.12, -69.59) * mm, "end": v(77.12, -70.28) * mm});
            skLineSegment(sketch, "E455", {"start": v(77.12, -70.28) * mm, "end": v(77.12, -70.98) * mm});
            skLineSegment(sketch, "E456", {"start": v(77.12, -70.98) * mm, "end": v(76.87, -73.06) * mm});
            skLineSegment(sketch, "E457", {"start": v(76.87, -73.06) * mm, "end": v(76.15, -75.56) * mm});
            skLineSegment(sketch, "E458", {"start": v(76.15, -75.56) * mm, "end": v(75, -77.77) * mm});
            skLineSegment(sketch, "E459", {"start": v(75, -77.77) * mm, "end": v(73.48, -79.64) * mm});
            skLineSegment(sketch, "E460", {"start": v(73.48, -79.64) * mm, "end": v(71.6, -81.15) * mm});
            skLineSegment(sketch, "E461", {"start": v(71.6, -81.15) * mm, "end": v(69.4, -82.27) * mm});
            skLineSegment(sketch, "E462", {"start": v(69.4, -82.27) * mm, "end": v(66.94, -82.97) * mm});
            skLineSegment(sketch, "E463", {"start": v(66.94, -82.97) * mm, "end": v(64.93, -83.2) * mm});
            skLineSegment(sketch, "E464", {"start": v(64.93, -83.2) * mm, "end": v(64.26, -83.2) * mm});
            skLineSegment(sketch, "E465", {"start": v(29.7, -83.2) * mm, "end": v(29, -83.2) * mm});
            skLineSegment(sketch, "E466", {"start": v(29, -83.2) * mm, "end": v(26.94, -82.96) * mm});
            skLineSegment(sketch, "E467", {"start": v(26.94, -82.96) * mm, "end": v(24.45, -82.24) * mm});
            skLineSegment(sketch, "E468", {"start": v(24.45, -82.24) * mm, "end": v(22.26, -81.09) * mm});
            skLineSegment(sketch, "E469", {"start": v(22.26, -81.09) * mm, "end": v(20.38, -79.55) * mm});
            skLineSegment(sketch, "E470", {"start": v(20.38, -79.55) * mm, "end": v(18.87, -77.66) * mm});
            skLineSegment(sketch, "E471", {"start": v(18.87, -77.66) * mm, "end": v(17.74, -75.46) * mm});
            skLineSegment(sketch, "E472", {"start": v(17.74, -75.46) * mm, "end": v(17.05, -72.99) * mm});
            skLineSegment(sketch, "E473", {"start": v(17.05, -72.99) * mm, "end": v(16.8, -70.96) * mm});
            skLineSegment(sketch, "E474", {"start": v(16.8, -70.96) * mm, "end": v(16.8, -70.28) * mm});
            skLineSegment(sketch, "E475", {"start": v(16.8, -70.28) * mm, "end": v(16.8, -69.6) * mm});
            skLineSegment(sketch, "E476", {"start": v(16.8, -69.6) * mm, "end": v(17.05, -67.57) * mm});
            skLineSegment(sketch, "E477", {"start": v(17.05, -67.57) * mm, "end": v(17.74, -65.09) * mm});
            skLineSegment(sketch, "E478", {"start": v(17.74, -65.09) * mm, "end": v(18.87, -62.88) * mm});
            skLineSegment(sketch, "E479", {"start": v(18.87, -62.88) * mm, "end": v(20.38, -60.98) * mm});
            skLineSegment(sketch, "E480", {"start": v(20.38, -60.98) * mm, "end": v(22.26, -59.44) * mm});
            skLineSegment(sketch, "E481", {"start": v(22.26, -59.44) * mm, "end": v(24.45, -58.29) * mm});
            skLineSegment(sketch, "E482", {"start": v(24.45, -58.29) * mm, "end": v(26.94, -57.57) * mm});
            skLineSegment(sketch, "E483", {"start": v(26.94, -57.57) * mm, "end": v(29, -57.32) * mm});
            skLineSegment(sketch, "E484", {"start": v(29, -57.32) * mm, "end": v(29.7, -57.32) * mm});
            skLineSegment(sketch, "E485", {"start": v(29.7, -57.32) * mm, "end": v(30.37, -57.32) * mm});
            skLineSegment(sketch, "E486", {"start": v(30.37, -57.32) * mm, "end": v(32.38, -57.56) * mm});
            skLineSegment(sketch, "E487", {"start": v(32.38, -57.56) * mm, "end": v(34.84, -58.26) * mm});
            skLineSegment(sketch, "E488", {"start": v(34.84, -58.26) * mm, "end": v(37.03, -59.38) * mm});
            skLineSegment(sketch, "E489", {"start": v(37.03, -59.38) * mm, "end": v(38.91, -60.9) * mm});
            skLineSegment(sketch, "E490", {"start": v(38.91, -60.9) * mm, "end": v(40.45, -62.78) * mm});
            skLineSegment(sketch, "E491", {"start": v(40.45, -62.78) * mm, "end": v(41.6, -65) * mm});
            skLineSegment(sketch, "E492", {"start": v(41.6, -65) * mm, "end": v(42.3, -67.5) * mm});
            skLineSegment(sketch, "E493", {"start": v(42.3, -67.5) * mm, "end": v(42.55, -69.59) * mm});
            skLineSegment(sketch, "E494", {"start": v(42.55, -69.59) * mm, "end": v(42.55, -70.28) * mm});
            skLineSegment(sketch, "E495", {"start": v(42.55, -70.28) * mm, "end": v(42.55, -70.98) * mm});
            skLineSegment(sketch, "E496", {"start": v(42.55, -70.98) * mm, "end": v(42.3, -73.06) * mm});
            skLineSegment(sketch, "E497", {"start": v(42.3, -73.06) * mm, "end": v(41.6, -75.56) * mm});
            skLineSegment(sketch, "E498", {"start": v(41.6, -75.56) * mm, "end": v(40.45, -77.77) * mm});
            skLineSegment(sketch, "E499", {"start": v(40.45, -77.77) * mm, "end": v(38.91, -79.64) * mm});
            skLineSegment(sketch, "E500", {"start": v(38.91, -79.64) * mm, "end": v(37.03, -81.15) * mm});
            skLineSegment(sketch, "E501", {"start": v(37.03, -81.15) * mm, "end": v(34.84, -82.27) * mm});
            skLineSegment(sketch, "E502", {"start": v(34.84, -82.27) * mm, "end": v(32.38, -82.97) * mm});
            skLineSegment(sketch, "E503", {"start": v(32.38, -82.97) * mm, "end": v(30.37, -83.2) * mm});
            skLineSegment(sketch, "E504", {"start": v(30.37, -83.2) * mm, "end": v(29.7, -83.2) * mm});
            skLineSegment(sketch, "E505", {"start": v(9.27, -62.13) * mm, "end": v(-2.55, -62.13) * mm});
            skLineSegment(sketch, "E506", {"start": v(-2.55, -62.13) * mm, "end": v(-2.55, -68.86) * mm});
            skLineSegment(sketch, "E507", {"start": v(-2.55, -68.86) * mm, "end": v(7.31, -68.86) * mm});
            skLineSegment(sketch, "E508", {"start": v(7.31, -68.86) * mm, "end": v(7.31, -73.34) * mm});
            skLineSegment(sketch, "E509", {"start": v(7.31, -73.34) * mm, "end": v(-2.55, -73.34) * mm});
            skLineSegment(sketch, "E510", {"start": v(-2.55, -73.34) * mm, "end": v(-2.55, -82.92) * mm});
            skLineSegment(sketch, "E511", {"start": v(-2.55, -82.92) * mm, "end": v(-7.5, -82.92) * mm});
            skLineSegment(sketch, "E512", {"start": v(-7.5, -82.92) * mm, "end": v(-7.5, -57.64) * mm});
            skLineSegment(sketch, "E513", {"start": v(-7.5, -57.64) * mm, "end": v(9.27, -57.64) * mm});
            skLineSegment(sketch, "E514", {"start": v(9.27, -57.64) * mm, "end": v(9.27, -62.13) * mm});
            skLineSegment(sketch, "E515", {"start": v(-21.41, -82.92) * mm, "end": v(-23.12, -77.87) * mm});
            skLineSegment(sketch, "E516", {"start": v(-23.12, -77.87) * mm, "end": v(-32.84, -77.87) * mm});
            skLineSegment(sketch, "E517", {"start": v(-32.84, -77.87) * mm, "end": v(-34.55, -82.92) * mm});
            skLineSegment(sketch, "E518", {"start": v(-34.55, -82.92) * mm, "end": v(-39.78, -82.92) * mm});
            skLineSegment(sketch, "E519", {"start": v(-39.78, -82.92) * mm, "end": v(-30.42, -57.64) * mm});
            skLineSegment(sketch, "E520", {"start": v(-30.42, -57.64) * mm, "end": v(-25.61, -57.64) * mm});
            skLineSegment(sketch, "E521", {"start": v(-25.61, -57.64) * mm, "end": v(-16.18, -82.92) * mm});
            skLineSegment(sketch, "E522", {"start": v(-16.18, -82.92) * mm, "end": v(-21.41, -82.92) * mm});
            skLineSegment(sketch, "E523", {"start": v(-47.46, -82.92) * mm, "end": v(-64.38, -82.92) * mm});
            skLineSegment(sketch, "E524", {"start": v(-64.38, -82.92) * mm, "end": v(-64.38, -57.64) * mm});
            skLineSegment(sketch, "E525", {"start": v(-64.38, -57.64) * mm, "end": v(-48.2, -57.64) * mm});
            skLineSegment(sketch, "E526", {"start": v(-48.2, -57.64) * mm, "end": v(-48.2, -62.13) * mm});
            skLineSegment(sketch, "E527", {"start": v(-48.2, -62.13) * mm, "end": v(-59.46, -62.13) * mm});
            skLineSegment(sketch, "E528", {"start": v(-59.46, -62.13) * mm, "end": v(-59.46, -68.18) * mm});
            skLineSegment(sketch, "E529", {"start": v(-59.46, -68.18) * mm, "end": v(-50.45, -68.18) * mm});
            skLineSegment(sketch, "E530", {"start": v(-50.45, -68.18) * mm, "end": v(-50.45, -72.6) * mm});
            skLineSegment(sketch, "E531", {"start": v(-50.45, -72.6) * mm, "end": v(-59.46, -72.6) * mm});
            skLineSegment(sketch, "E532", {"start": v(-59.46, -72.6) * mm, "end": v(-59.46, -78.47) * mm});
            skLineSegment(sketch, "E533", {"start": v(-59.46, -78.47) * mm, "end": v(-47.46, -78.47) * mm});
            skLineSegment(sketch, "E534", {"start": v(-47.46, -78.47) * mm, "end": v(-47.46, -82.92) * mm});
            skLineSegment(sketch, "E535", {"start": v(-82.88, -83.2) * mm, "end": v(-83.5, -83.2) * mm});
            skLineSegment(sketch, "E536", {"start": v(-83.5, -83.2) * mm, "end": v(-85.33, -82.97) * mm});
            skLineSegment(sketch, "E537", {"start": v(-85.33, -82.97) * mm, "end": v(-87.73, -82.24) * mm});
            skLineSegment(sketch, "E538", {"start": v(-87.73, -82.24) * mm, "end": v(-90.01, -81) * mm});
            skLineSegment(sketch, "E539", {"start": v(-90.01, -81) * mm, "end": v(-91.63, -79.71) * mm});
            skLineSegment(sketch, "E540", {"start": v(-91.63, -79.71) * mm, "end": v(-92.1, -79.22) * mm});
            skLineSegment(sketch, "E541", {"start": v(-92.1, -79.22) * mm, "end": v(-89.11, -75.52) * mm});
            skLineSegment(sketch, "E542", {"start": v(-89.11, -75.52) * mm, "end": v(-88.64, -76.07) * mm});
            skLineSegment(sketch, "E543", {"start": v(-88.64, -76.07) * mm, "end": v(-86, -77.93) * mm});
            skLineSegment(sketch, "E544", {"start": v(-86, -77.93) * mm, "end": v(-83.6, -78.69) * mm});
            skLineSegment(sketch, "E545", {"start": v(-83.6, -78.69) * mm, "end": v(-82.81, -78.69) * mm});
            skLineSegment(sketch, "E546", {"start": v(-82.81, -78.69) * mm, "end": v(-82.41, -78.69) * mm});
            skLineSegment(sketch, "E547", {"start": v(-82.41, -78.69) * mm, "end": v(-81.22, -78.49) * mm});
            skLineSegment(sketch, "E548", {"start": v(-81.22, -78.49) * mm, "end": v(-80.09, -77.94) * mm});
            skLineSegment(sketch, "E549", {"start": v(-80.09, -77.94) * mm, "end": v(-79.4, -77.1) * mm});
            skLineSegment(sketch, "E550", {"start": v(-79.4, -77.1) * mm, "end": v(-79.18, -76.28) * mm});
            skLineSegment(sketch, "E551", {"start": v(-79.18, -76.28) * mm, "end": v(-79.18, -76.01) * mm});
            skLineSegment(sketch, "E552", {"start": v(-79.18, -76.01) * mm, "end": v(-79.18, -75.72) * mm});
            skLineSegment(sketch, "E553", {"start": v(-79.18, -75.72) * mm, "end": v(-79.44, -74.82) * mm});
            skLineSegment(sketch, "E554", {"start": v(-79.44, -74.82) * mm, "end": v(-80.24, -73.93) * mm});
            skLineSegment(sketch, "E555", {"start": v(-80.24, -73.93) * mm, "end": v(-81.61, -73.19) * mm});
            skLineSegment(sketch, "E556", {"start": v(-81.61, -73.19) * mm, "end": v(-83.1, -72.62) * mm});
            skLineSegment(sketch, "E557", {"start": v(-83.1, -72.62) * mm, "end": v(-83.6, -72.45) * mm});
            skLineSegment(sketch, "E558", {"start": v(-83.6, -72.45) * mm, "end": v(-84.3, -72.2) * mm});
            skLineSegment(sketch, "E559", {"start": v(-84.3, -72.2) * mm, "end": v(-86.4, -71.32) * mm});
            skLineSegment(sketch, "E560", {"start": v(-86.4, -71.32) * mm, "end": v(-88.83, -69.78) * mm});
            skLineSegment(sketch, "E561", {"start": v(-88.83, -69.78) * mm, "end": v(-90.56, -67.6) * mm});
            skLineSegment(sketch, "E562", {"start": v(-90.56, -67.6) * mm, "end": v(-91.21, -65.31) * mm});
            skLineSegment(sketch, "E563", {"start": v(-91.21, -65.31) * mm, "end": v(-91.21, -64.55) * mm});
            skLineSegment(sketch, "E564", {"start": v(-91.21, -64.55) * mm, "end": v(-91.21, -63.84) * mm});
            skLineSegment(sketch, "E565", {"start": v(-91.21, -63.84) * mm, "end": v(-90.59, -61.72) * mm});
            skLineSegment(sketch, "E566", {"start": v(-90.59, -61.72) * mm, "end": v(-88.86, -59.44) * mm});
            skLineSegment(sketch, "E567", {"start": v(-88.86, -59.44) * mm, "end": v(-86.29, -57.91) * mm});
            skLineSegment(sketch, "E568", {"start": v(-86.29, -57.91) * mm, "end": v(-83.9, -57.33) * mm});
            skLineSegment(sketch, "E569", {"start": v(-83.9, -57.33) * mm, "end": v(-83.1, -57.32) * mm});
            skLineSegment(sketch, "E570", {"start": v(-83.1, -57.32) * mm, "end": v(-82.31, -57.31) * mm});
            skLineSegment(sketch, "E571", {"start": v(-82.31, -57.31) * mm, "end": v(-78.59, -58.14) * mm});
            skLineSegment(sketch, "E572", {"start": v(-78.59, -58.14) * mm, "end": v(-75.2, -60) * mm});
            skLineSegment(sketch, "E573", {"start": v(-75.2, -60) * mm, "end": v(-74.59, -60.53) * mm});
            skLineSegment(sketch, "E574", {"start": v(-74.59, -60.53) * mm, "end": v(-77.47, -64.3) * mm});
            skLineSegment(sketch, "E575", {"start": v(-77.47, -64.3) * mm, "end": v(-77.84, -64) * mm});
            skLineSegment(sketch, "E576", {"start": v(-77.84, -64) * mm, "end": v(-79, -63.17) * mm});
            skLineSegment(sketch, "E577", {"start": v(-79, -63.17) * mm, "end": v(-80.43, -62.4) * mm});
            skLineSegment(sketch, "E578", {"start": v(-80.43, -62.4) * mm, "end": v(-81.76, -61.95) * mm});
            skLineSegment(sketch, "E579", {"start": v(-81.76, -61.95) * mm, "end": v(-82.68, -61.8) * mm});
            skLineSegment(sketch, "E580", {"start": v(-82.68, -61.8) * mm, "end": v(-82.99, -61.8) * mm});
            skLineSegment(sketch, "E581", {"start": v(-82.99, -61.8) * mm, "end": v(-83.3, -61.8) * mm});
            skLineSegment(sketch, "E582", {"start": v(-83.3, -61.8) * mm, "end": v(-84.2, -61.98) * mm});
            skLineSegment(sketch, "E583", {"start": v(-84.2, -61.98) * mm, "end": v(-85.16, -62.47) * mm});
            skLineSegment(sketch, "E584", {"start": v(-85.16, -62.47) * mm, "end": v(-85.79, -63.26) * mm});
            skLineSegment(sketch, "E585", {"start": v(-85.79, -63.26) * mm, "end": v(-86.01, -64.07) * mm});
            skLineSegment(sketch, "E586", {"start": v(-86.01, -64.07) * mm, "end": v(-86.01, -64.33) * mm});
            skLineSegment(sketch, "E587", {"start": v(-86.01, -64.33) * mm, "end": v(-86.02, -64.59) * mm});
            skLineSegment(sketch, "E588", {"start": v(-86.02, -64.59) * mm, "end": v(-85.77, -65.36) * mm});
            skLineSegment(sketch, "E589", {"start": v(-85.77, -65.36) * mm, "end": v(-85, -66.19) * mm});
            skLineSegment(sketch, "E590", {"start": v(-85, -66.19) * mm, "end": v(-83.66, -66.93) * mm});
            skLineSegment(sketch, "E591", {"start": v(-83.66, -66.93) * mm, "end": v(-82.25, -67.53) * mm});
            skLineSegment(sketch, "E592", {"start": v(-82.25, -67.53) * mm, "end": v(-81.78, -67.72) * mm});
            skLineSegment(sketch, "E593", {"start": v(-81.78, -67.72) * mm, "end": v(-81, -68.02) * mm});
            skLineSegment(sketch, "E594", {"start": v(-81, -68.02) * mm, "end": v(-78.7, -68.96) * mm});
            skLineSegment(sketch, "E595", {"start": v(-78.7, -68.96) * mm, "end": v(-76.22, -70.4) * mm});
            skLineSegment(sketch, "E596", {"start": v(-76.22, -70.4) * mm, "end": v(-74.55, -72.42) * mm});
            skLineSegment(sketch, "E597", {"start": v(-74.55, -72.42) * mm, "end": v(-73.94, -74.69) * mm});
            skLineSegment(sketch, "E598", {"start": v(-73.94, -74.69) * mm, "end": v(-73.94, -75.44) * mm});
            skLineSegment(sketch, "E599", {"start": v(-73.94, -75.44) * mm, "end": v(-73.94, -75.92) * mm});
            skLineSegment(sketch, "E600", {"start": v(-73.94, -75.92) * mm, "end": v(-74.16, -77.36) * mm});
            skLineSegment(sketch, "E601", {"start": v(-74.16, -77.36) * mm, "end": v(-74.76, -78.99) * mm});
            skLineSegment(sketch, "E602", {"start": v(-74.76, -78.99) * mm, "end": v(-75.68, -80.33) * mm});
            skLineSegment(sketch, "E603", {"start": v(-75.68, -80.33) * mm, "end": v(-76.86, -81.4) * mm});
            skLineSegment(sketch, "E604", {"start": v(-76.86, -81.4) * mm, "end": v(-78.24, -82.2) * mm});
            skLineSegment(sketch, "E605", {"start": v(-78.24, -82.2) * mm, "end": v(-79.74, -82.77) * mm});
            skLineSegment(sketch, "E606", {"start": v(-79.74, -82.77) * mm, "end": v(-81.31, -83.1) * mm});
            skLineSegment(sketch, "E607", {"start": v(-81.31, -83.1) * mm, "end": v(-82.49, -83.2) * mm});
            skLineSegment(sketch, "E608", {"start": v(-82.49, -83.2) * mm, "end": v(-82.88, -83.2) * mm});
            skLineSegment(sketch, "E609", {"start": v(-94.6, -29.9) * mm, "end": v(-105.92, -0.74) * mm});
            skLineSegment(sketch, "E610", {"start": v(-105.92, -0.74) * mm, "end": v(-157.3, -0.74) * mm});
            skLineSegment(sketch, "E611", {"start": v(-157.3, -0.74) * mm, "end": v(-168.63, -29.9) * mm});
            skLineSegment(sketch, "E612", {"start": v(-168.63, -29.9) * mm, "end": v(-168.67, -30) * mm});
            skLineSegment(sketch, "E613", {"start": v(-168.67, -30) * mm, "end": v(-169.03, -30.38) * mm});
            skLineSegment(sketch, "E614", {"start": v(-169.03, -30.38) * mm, "end": v(-169.46, -30.58) * mm});
            skLineSegment(sketch, "E615", {"start": v(-169.46, -30.58) * mm, "end": v(-169.61, -30.58) * mm});
            skLineSegment(sketch, "E616", {"start": v(-169.61, -30.58) * mm, "end": v(-180, -30.58) * mm});
            skLineSegment(sketch, "E617", {"start": v(-180, -30.58) * mm, "end": v(-180, -30.58) * mm});
            skLineSegment(sketch, "E618", {"start": v(-180, -30.58) * mm, "end": v(-187.48, -30.58) * mm});
            skLineSegment(sketch, "E619", {"start": v(-187.48, -30.58) * mm, "end": v(-187.6, -30.58) * mm});
            skLineSegment(sketch, "E620", {"start": v(-187.6, -30.58) * mm, "end": v(-187.93, -30.47) * mm});
            skLineSegment(sketch, "E621", {"start": v(-187.93, -30.47) * mm, "end": v(-188.23, -30.24) * mm});
            skLineSegment(sketch, "E622", {"start": v(-188.23, -30.24) * mm, "end": v(-188.28, -30.18) * mm});
            skLineSegment(sketch, "E623", {"start": v(-188.28, -30.18) * mm, "end": v(-188.32, -30.12) * mm});
            skLineSegment(sketch, "E624", {"start": v(-188.32, -30.12) * mm, "end": v(-188.44, -29.39) * mm});
            skLineSegment(sketch, "E625", {"start": v(-188.44, -29.39) * mm, "end": v(-188.41, -29.31) * mm});
            skLineSegment(sketch, "E626", {"start": v(-188.41, -29.31) * mm, "end": v(-183.07, -13.62) * mm});
            skLineSegment(sketch, "E627", {"start": v(-183.07, -13.62) * mm, "end": v(-180.14, -13.62) * mm});
            skLineSegment(sketch, "E628", {"start": v(-180.14, -13.62) * mm, "end": v(-180.14, -13.62) * mm});
            skLineSegment(sketch, "E629", {"start": v(-180.14, -13.62) * mm, "end": v(-149.74, 64.64) * mm});
            skLineSegment(sketch, "E630", {"start": v(-149.74, 64.64) * mm, "end": v(-152.15, 64.64) * mm});
            skLineSegment(sketch, "E631", {"start": v(-152.15, 64.64) * mm, "end": v(-157.62, 80.7) * mm});
            skLineSegment(sketch, "E632", {"start": v(-157.62, 80.7) * mm, "end": v(-157.64, 80.76) * mm});
            skLineSegment(sketch, "E633", {"start": v(-157.64, 80.76) * mm, "end": v(-157.56, 81.27) * mm});
            skLineSegment(sketch, "E634", {"start": v(-157.56, 81.27) * mm, "end": v(-157.53, 81.32) * mm});
            skLineSegment(sketch, "E635", {"start": v(-157.53, 81.32) * mm, "end": v(-157.5, 81.36) * mm});
            skLineSegment(sketch, "E636", {"start": v(-157.5, 81.36) * mm, "end": v(-157.1, 81.6) * mm});
            skLineSegment(sketch, "E637", {"start": v(-157.1, 81.6) * mm, "end": v(-156.96, 81.6) * mm});
            skLineSegment(sketch, "E638", {"start": v(-156.96, 81.6) * mm, "end": v(-143.15, 81.6) * mm});
            skLineSegment(sketch, "E639", {"start": v(-143.15, 81.6) * mm, "end": v(-143.15, 81.6) * mm});
            skLineSegment(sketch, "E640", {"start": v(-143.15, 81.6) * mm, "end": v(-131.61, 81.6) * mm});
            skLineSegment(sketch, "E641", {"start": v(-131.61, 81.6) * mm, "end": v(-120.08, 81.6) * mm});
            skLineSegment(sketch, "E642", {"start": v(-120.08, 81.6) * mm, "end": v(-113.49, 64.64) * mm});
            skLineSegment(sketch, "E643", {"start": v(-113.49, 64.64) * mm, "end": v(-83.09, -13.62) * mm});
            skLineSegment(sketch, "E644", {"start": v(-83.09, -13.62) * mm, "end": v(-77.18, -28.82) * mm});
            skLineSegment(sketch, "E645", {"start": v(-77.18, -28.82) * mm, "end": v(-77.13, -28.97) * mm});
            skLineSegment(sketch, "E646", {"start": v(-77.13, -28.97) * mm, "end": v(-77.1, -29.46) * mm});
            skLineSegment(sketch, "E647", {"start": v(-77.1, -29.46) * mm, "end": v(-77.34, -30.02) * mm});
            skLineSegment(sketch, "E648", {"start": v(-77.34, -30.02) * mm, "end": v(-77.82, -30.42) * mm});
            skLineSegment(sketch, "E649", {"start": v(-77.82, -30.42) * mm, "end": v(-78.3, -30.58) * mm});
            skLineSegment(sketch, "E650", {"start": v(-78.3, -30.58) * mm, "end": v(-78.47, -30.58) * mm});
            skLineSegment(sketch, "E651", {"start": v(-78.47, -30.58) * mm, "end": v(-93.57, -30.58) * mm});
            skLineSegment(sketch, "E652", {"start": v(-93.57, -30.58) * mm, "end": v(-93.72, -30.58) * mm});
            skLineSegment(sketch, "E653", {"start": v(-93.72, -30.58) * mm, "end": v(-94.19, -30.38) * mm});
            skLineSegment(sketch, "E654", {"start": v(-94.19, -30.38) * mm, "end": v(-94.56, -30) * mm});
            skLineSegment(sketch, "E655", {"start": v(-94.56, -30) * mm, "end": v(-94.6, -29.9) * mm});
            skLineSegment(sketch, "E656", {"start": v(-94.6, -29.9) * mm, "end": v(-94.6, -29.9) * mm});
            skLineSegment(sketch, "E657", {"start": v(-164.42, -62.07) * mm, "end": v(-164, -61.9) * mm});
            skLineSegment(sketch, "E658", {"start": v(-164, -61.9) * mm, "end": v(-159.72, -60.4) * mm});
            skLineSegment(sketch, "E659", {"start": v(-159.72, -60.4) * mm, "end": v(-159.3, -60.28) * mm});
            skLineSegment(sketch, "E660", {"start": v(-159.3, -60.28) * mm, "end": v(-159.08, -60.17) * mm});
            skLineSegment(sketch, "E661", {"start": v(-159.08, -60.17) * mm, "end": v(-158.02, -60.05) * mm});
            skLineSegment(sketch, "E662", {"start": v(-158.02, -60.05) * mm, "end": v(-156.95, -60.1) * mm});
            skLineSegment(sketch, "E663", {"start": v(-156.95, -60.1) * mm, "end": v(-156.73, -60.09) * mm});
            skLineSegment(sketch, "E664", {"start": v(-156.73, -60.09) * mm, "end": v(-153.53, -60.09) * mm});
            skLineSegment(sketch, "E665", {"start": v(-153.53, -60.09) * mm, "end": v(-153, -60.47) * mm});
            skLineSegment(sketch, "E666", {"start": v(-153, -60.47) * mm, "end": v(-146.58, -65.14) * mm});
            skLineSegment(sketch, "E667", {"start": v(-146.58, -65.14) * mm, "end": v(-149.95, -67.59) * mm});
            skLineSegment(sketch, "E668", {"start": v(-149.95, -67.59) * mm, "end": v(-154.82, -64.05) * mm});
            skLineSegment(sketch, "E669", {"start": v(-154.82, -64.05) * mm, "end": v(-156.73, -64.05) * mm});
            skLineSegment(sketch, "E670", {"start": v(-156.73, -64.05) * mm, "end": v(-156.95, -64.03) * mm});
            skLineSegment(sketch, "E671", {"start": v(-156.95, -64.03) * mm, "end": v(-158.02, -64.09) * mm});
            skLineSegment(sketch, "E672", {"start": v(-158.02, -64.09) * mm, "end": v(-159.08, -63.97) * mm});
            skLineSegment(sketch, "E673", {"start": v(-159.08, -63.97) * mm, "end": v(-159.3, -63.86) * mm});
            skLineSegment(sketch, "E674", {"start": v(-159.3, -63.86) * mm, "end": v(-159.72, -63.73) * mm});
            skLineSegment(sketch, "E675", {"start": v(-159.72, -63.73) * mm, "end": v(-164, -62.25) * mm});
            skLineSegment(sketch, "E676", {"start": v(-164, -62.25) * mm, "end": v(-164.42, -62.07) * mm});
            skLineSegment(sketch, "E677", {"start": v(-127.94, -63.84) * mm, "end": v(-128.16, -63.94) * mm});
            skLineSegment(sketch, "E678", {"start": v(-128.16, -63.94) * mm, "end": v(-129.22, -64.08) * mm});
            skLineSegment(sketch, "E679", {"start": v(-129.22, -64.08) * mm, "end": v(-130.3, -64.04) * mm});
            skLineSegment(sketch, "E680", {"start": v(-130.3, -64.04) * mm, "end": v(-130.5, -64.05) * mm});
            skLineSegment(sketch, "E681", {"start": v(-130.5, -64.05) * mm, "end": v(-132.42, -64.05) * mm});
            skLineSegment(sketch, "E682", {"start": v(-132.42, -64.05) * mm, "end": v(-153, -79) * mm});
            skLineSegment(sketch, "E683", {"start": v(-153, -79) * mm, "end": v(-153.53, -79.38) * mm});
            skLineSegment(sketch, "E684", {"start": v(-153.53, -79.38) * mm, "end": v(-156.73, -79.38) * mm});
            skLineSegment(sketch, "E685", {"start": v(-156.73, -79.38) * mm, "end": v(-156.95, -79.37) * mm});
            skLineSegment(sketch, "E686", {"start": v(-156.95, -79.37) * mm, "end": v(-158.02, -79.42) * mm});
            skLineSegment(sketch, "E687", {"start": v(-158.02, -79.42) * mm, "end": v(-159.08, -79.3) * mm});
            skLineSegment(sketch, "E688", {"start": v(-159.08, -79.3) * mm, "end": v(-159.3, -79.2) * mm});
            skLineSegment(sketch, "E689", {"start": v(-159.3, -79.2) * mm, "end": v(-159.72, -79.06) * mm});
            skLineSegment(sketch, "E690", {"start": v(-159.72, -79.06) * mm, "end": v(-164, -77.58) * mm});
            skLineSegment(sketch, "E691", {"start": v(-164, -77.58) * mm, "end": v(-164.42, -77.4) * mm});
            skLineSegment(sketch, "E692", {"start": v(-164.42, -77.4) * mm, "end": v(-164, -77.22) * mm});
            skLineSegment(sketch, "E693", {"start": v(-164, -77.22) * mm, "end": v(-159.72, -75.74) * mm});
            skLineSegment(sketch, "E694", {"start": v(-159.72, -75.74) * mm, "end": v(-159.3, -75.6) * mm});
            skLineSegment(sketch, "E695", {"start": v(-159.3, -75.6) * mm, "end": v(-159.08, -75.5) * mm});
            skLineSegment(sketch, "E696", {"start": v(-159.08, -75.5) * mm, "end": v(-158.02, -75.38) * mm});
            skLineSegment(sketch, "E697", {"start": v(-158.02, -75.38) * mm, "end": v(-156.95, -75.44) * mm});
            skLineSegment(sketch, "E698", {"start": v(-156.95, -75.44) * mm, "end": v(-156.73, -75.42) * mm});
            skLineSegment(sketch, "E699", {"start": v(-156.73, -75.42) * mm, "end": v(-154.81, -75.42) * mm});
            skLineSegment(sketch, "E700", {"start": v(-154.81, -75.42) * mm, "end": v(-134.23, -60.47) * mm});
            skLineSegment(sketch, "E701", {"start": v(-134.23, -60.47) * mm, "end": v(-133.71, -60.09) * mm});
            skLineSegment(sketch, "E702", {"start": v(-133.71, -60.09) * mm, "end": v(-130.5, -60.09) * mm});
            skLineSegment(sketch, "E703", {"start": v(-130.5, -60.09) * mm, "end": v(-130.3, -60.1) * mm});
            skLineSegment(sketch, "E704", {"start": v(-130.3, -60.1) * mm, "end": v(-129.22, -60.06) * mm});
            skLineSegment(sketch, "E705", {"start": v(-129.22, -60.06) * mm, "end": v(-128.16, -60.2) * mm});
            skLineSegment(sketch, "E706", {"start": v(-128.16, -60.2) * mm, "end": v(-127.94, -60.3) * mm});
            skLineSegment(sketch, "E707", {"start": v(-127.94, -60.3) * mm, "end": v(-127.52, -60.43) * mm});
            skLineSegment(sketch, "E708", {"start": v(-127.52, -60.43) * mm, "end": v(-123.25, -61.9) * mm});
            skLineSegment(sketch, "E709", {"start": v(-123.25, -61.9) * mm, "end": v(-122.82, -62.07) * mm});
            skLineSegment(sketch, "E710", {"start": v(-122.82, -62.07) * mm, "end": v(-123.25, -62.24) * mm});
            skLineSegment(sketch, "E711", {"start": v(-123.25, -62.24) * mm, "end": v(-127.52, -63.7) * mm});
            skLineSegment(sketch, "E712", {"start": v(-127.52, -63.7) * mm, "end": v(-127.94, -63.84) * mm});
            skLineSegment(sketch, "E713", {"start": v(-127.94, -79.17) * mm, "end": v(-128.16, -79.27) * mm});
            skLineSegment(sketch, "E714", {"start": v(-128.16, -79.27) * mm, "end": v(-129.22, -79.4) * mm});
            skLineSegment(sketch, "E715", {"start": v(-129.22, -79.4) * mm, "end": v(-130.3, -79.37) * mm});
            skLineSegment(sketch, "E716", {"start": v(-130.3, -79.37) * mm, "end": v(-130.5, -79.38) * mm});
            skLineSegment(sketch, "E717", {"start": v(-130.5, -79.38) * mm, "end": v(-133.71, -79.38) * mm});
            skLineSegment(sketch, "E718", {"start": v(-133.71, -79.38) * mm, "end": v(-134.23, -79) * mm});
            skLineSegment(sketch, "E719", {"start": v(-134.23, -79) * mm, "end": v(-140.67, -74.33) * mm});
            skLineSegment(sketch, "E720", {"start": v(-140.67, -74.33) * mm, "end": v(-137.3, -71.88) * mm});
            skLineSegment(sketch, "E721", {"start": v(-137.3, -71.88) * mm, "end": v(-132.42, -75.42) * mm});
            skLineSegment(sketch, "E722", {"start": v(-132.42, -75.42) * mm, "end": v(-130.5, -75.42) * mm});
            skLineSegment(sketch, "E723", {"start": v(-130.5, -75.42) * mm, "end": v(-130.3, -75.43) * mm});
            skLineSegment(sketch, "E724", {"start": v(-130.3, -75.43) * mm, "end": v(-129.22, -75.4) * mm});
            skLineSegment(sketch, "E725", {"start": v(-129.22, -75.4) * mm, "end": v(-128.16, -75.53) * mm});
            skLineSegment(sketch, "E726", {"start": v(-128.16, -75.53) * mm, "end": v(-127.94, -75.64) * mm});
            skLineSegment(sketch, "E727", {"start": v(-127.94, -75.64) * mm, "end": v(-127.52, -75.76) * mm});
            skLineSegment(sketch, "E728", {"start": v(-127.52, -75.76) * mm, "end": v(-123.25, -77.23) * mm});
            skLineSegment(sketch, "E729", {"start": v(-123.25, -77.23) * mm, "end": v(-122.82, -77.4) * mm});
            skLineSegment(sketch, "E730", {"start": v(-122.82, -77.4) * mm, "end": v(-123.25, -77.57) * mm});
            skLineSegment(sketch, "E731", {"start": v(-123.25, -77.57) * mm, "end": v(-127.52, -79.04) * mm});
            skLineSegment(sketch, "E732", {"start": v(-127.52, -79.04) * mm, "end": v(-127.94, -79.17) * mm});
            skLineSegment(sketch, "E733", {"start": v(-198.18, -82.92) * mm, "end": v(-204.91, -72.77) * mm});
            skLineSegment(sketch, "E734", {"start": v(-204.91, -72.77) * mm, "end": v(-204.95, -72.77) * mm});
            skLineSegment(sketch, "E735", {"start": v(-204.95, -72.77) * mm, "end": v(-207.44, -75.73) * mm});
            skLineSegment(sketch, "E736", {"start": v(-207.44, -75.73) * mm, "end": v(-207.44, -82.92) * mm});
            skLineSegment(sketch, "E737", {"start": v(-207.44, -82.92) * mm, "end": v(-212.42, -82.92) * mm});
            skLineSegment(sketch, "E738", {"start": v(-212.42, -82.92) * mm, "end": v(-212.42, -57.64) * mm});
            skLineSegment(sketch, "E739", {"start": v(-212.42, -57.64) * mm, "end": v(-207.44, -57.64) * mm});
            skLineSegment(sketch, "E740", {"start": v(-207.44, -57.64) * mm, "end": v(-207.44, -68.78) * mm});
            skLineSegment(sketch, "E741", {"start": v(-207.44, -68.78) * mm, "end": v(-207.4, -68.78) * mm});
            skLineSegment(sketch, "E742", {"start": v(-207.4, -68.78) * mm, "end": v(-198.64, -57.64) * mm});
            skLineSegment(sketch, "E743", {"start": v(-198.64, -57.64) * mm, "end": v(-192.3, -57.64) * mm});
            skLineSegment(sketch, "E744", {"start": v(-192.3, -57.64) * mm, "end": v(-201.63, -68.78) * mm});
            skLineSegment(sketch, "E745", {"start": v(-201.63, -68.78) * mm, "end": v(-192.02, -82.92) * mm});
            skLineSegment(sketch, "E746", {"start": v(-192.02, -82.92) * mm, "end": v(-198.18, -82.92) * mm});
            skLineSegment(sketch, "E747", {"start": v(-226.33, -82.92) * mm, "end": v(-228.04, -77.87) * mm});
            skLineSegment(sketch, "E748", {"start": v(-228.04, -77.87) * mm, "end": v(-237.76, -77.87) * mm});
            skLineSegment(sketch, "E749", {"start": v(-237.76, -77.87) * mm, "end": v(-239.47, -82.92) * mm});
            skLineSegment(sketch, "E750", {"start": v(-239.47, -82.92) * mm, "end": v(-244.7, -82.92) * mm});
            skLineSegment(sketch, "E751", {"start": v(-244.7, -82.92) * mm, "end": v(-235.34, -57.64) * mm});
            skLineSegment(sketch, "E752", {"start": v(-235.34, -57.64) * mm, "end": v(-230.53, -57.64) * mm});
            skLineSegment(sketch, "E753", {"start": v(-230.53, -57.64) * mm, "end": v(-221.1, -82.92) * mm});
            skLineSegment(sketch, "E754", {"start": v(-221.1, -82.92) * mm, "end": v(-226.33, -82.92) * mm});
            skLineSegment(sketch, "E755", {"start": v(-265.64, 8.74) * mm, "end": v(-297.01, 8.72) * mm});
            skLineSegment(sketch, "E756", {"start": v(-297.01, 8.72) * mm, "end": v(-297.2, 8.72) * mm});
            skLineSegment(sketch, "E757", {"start": v(-297.2, 8.72) * mm, "end": v(-297.73, 8.42) * mm});
            skLineSegment(sketch, "E758", {"start": v(-297.73, 8.42) * mm, "end": v(-298.03, 7.88) * mm});
            skLineSegment(sketch, "E759", {"start": v(-298.03, 7.88) * mm, "end": v(-298.03, 7.7) * mm});
            skLineSegment(sketch, "E760", {"start": v(-298.03, 7.7) * mm, "end": v(-298.02, -28.24) * mm});
            skLineSegment(sketch, "E761", {"start": v(-298.02, -28.24) * mm, "end": v(-298.02, -28.45) * mm});
            skLineSegment(sketch, "E762", {"start": v(-298.02, -28.45) * mm, "end": v(-298.2, -29.09) * mm});
            skLineSegment(sketch, "E763", {"start": v(-298.2, -29.09) * mm, "end": v(-298.66, -29.79) * mm});
            skLineSegment(sketch, "E764", {"start": v(-298.66, -29.79) * mm, "end": v(-299.35, -30.25) * mm});
            skLineSegment(sketch, "E765", {"start": v(-299.35, -30.25) * mm, "end": v(-300, -30.43) * mm});
            skLineSegment(sketch, "E766", {"start": v(-300, -30.43) * mm, "end": v(-300.2, -30.43) * mm});
            skLineSegment(sketch, "E767", {"start": v(-300.2, -30.43) * mm, "end": v(-321.2, -30.43) * mm});
            skLineSegment(sketch, "E768", {"start": v(-321.2, -30.43) * mm, "end": v(-321.39, -30.43) * mm});
            skLineSegment(sketch, "E769", {"start": v(-321.39, -30.43) * mm, "end": v(-321.94, -30.25) * mm});
            skLineSegment(sketch, "E770", {"start": v(-321.94, -30.25) * mm, "end": v(-322.44, -29.86) * mm});
            skLineSegment(sketch, "E771", {"start": v(-322.44, -29.86) * mm, "end": v(-322.51, -29.76) * mm});
            skLineSegment(sketch, "E772", {"start": v(-322.51, -29.76) * mm, "end": v(-322.6, -29.65) * mm});
            skLineSegment(sketch, "E773", {"start": v(-322.6, -29.65) * mm, "end": v(-322.8, -29.06) * mm});
            skLineSegment(sketch, "E774", {"start": v(-322.8, -29.06) * mm, "end": v(-322.78, -28.43) * mm});
            skLineSegment(sketch, "E775", {"start": v(-322.78, -28.43) * mm, "end": v(-322.73, -28.3) * mm});
            skLineSegment(sketch, "E776", {"start": v(-322.73, -28.3) * mm, "end": v(-317.79, -13.47) * mm});
            skLineSegment(sketch, "E777", {"start": v(-317.79, -13.47) * mm, "end": v(-315, -13.47) * mm});
            skLineSegment(sketch, "E778", {"start": v(-315, -13.47) * mm, "end": v(-315, 64.8) * mm});
            skLineSegment(sketch, "E779", {"start": v(-315, 64.8) * mm, "end": v(-317.79, 64.8) * mm});
            skLineSegment(sketch, "E780", {"start": v(-317.79, 64.8) * mm, "end": v(-323.04, 80.55) * mm});
            skLineSegment(sketch, "E781", {"start": v(-323.04, 80.55) * mm, "end": v(-323.06, 80.6) * mm});
            skLineSegment(sketch, "E782", {"start": v(-323.06, 80.6) * mm, "end": v(-323.08, 80.8) * mm});
            skLineSegment(sketch, "E783", {"start": v(-323.08, 80.8) * mm, "end": v(-323.03, 80.9) * mm});
            skLineSegment(sketch, "E784", {"start": v(-323.03, 80.9) * mm, "end": v(-323.03, 80.91) * mm});
            skLineSegment(sketch, "E785", {"start": v(-323.03, 80.91) * mm, "end": v(-323, 80.96) * mm});
            skLineSegment(sketch, "E786", {"start": v(-323, 80.96) * mm, "end": v(-322.77, 81.12) * mm});
            skLineSegment(sketch, "E787", {"start": v(-322.77, 81.12) * mm, "end": v(-322.04, 81.4) * mm});
            skLineSegment(sketch, "E788", {"start": v(-322.04, 81.4) * mm, "end": v(-320.63, 81.65) * mm});
            skLineSegment(sketch, "E789", {"start": v(-320.63, 81.65) * mm, "end": v(-318.87, 81.75) * mm});
            skLineSegment(sketch, "E790", {"start": v(-318.87, 81.75) * mm, "end": v(-318.3, 81.75) * mm});
            skLineSegment(sketch, "E791", {"start": v(-318.3, 81.75) * mm, "end": v(-250.59, 81.75) * mm});
            skLineSegment(sketch, "E792", {"start": v(-250.59, 81.75) * mm, "end": v(-249.65, 81.75) * mm});
            skLineSegment(sketch, "E793", {"start": v(-249.65, 81.75) * mm, "end": v(-246.85, 81.58) * mm});
            skLineSegment(sketch, "E794", {"start": v(-246.85, 81.58) * mm, "end": v(-243.2, 81.08) * mm});
            skLineSegment(sketch, "E795", {"start": v(-243.2, 81.08) * mm, "end": v(-239.65, 80.25) * mm});
            skLineSegment(sketch, "E796", {"start": v(-239.65, 80.25) * mm, "end": v(-236.22, 79.13) * mm});
            skLineSegment(sketch, "E797", {"start": v(-236.22, 79.13) * mm, "end": v(-232.94, 77.72) * mm});
            skLineSegment(sketch, "E798", {"start": v(-232.94, 77.72) * mm, "end": v(-229.8, 76.04) * mm});
            skLineSegment(sketch, "E799", {"start": v(-229.8, 76.04) * mm, "end": v(-226.86, 74.1) * mm});
            skLineSegment(sketch, "E800", {"start": v(-226.86, 74.1) * mm, "end": v(-224.1, 71.93) * mm});
            skLineSegment(sketch, "E801", {"start": v(-224.1, 71.93) * mm, "end": v(-221.56, 69.54) * mm});
            skLineSegment(sketch, "E802", {"start": v(-221.56, 69.54) * mm, "end": v(-219.25, 66.94) * mm});
            skLineSegment(sketch, "E803", {"start": v(-219.25, 66.94) * mm, "end": v(-217.2, 64.14) * mm});
            skLineSegment(sketch, "E804", {"start": v(-217.2, 64.14) * mm, "end": v(-215.4, 61.17) * mm});
            skLineSegment(sketch, "E805", {"start": v(-215.4, 61.17) * mm, "end": v(-213.9, 58.05) * mm});
            skLineSegment(sketch, "E806", {"start": v(-213.9, 58.05) * mm, "end": v(-212.7, 54.77) * mm});
            skLineSegment(sketch, "E807", {"start": v(-212.7, 54.77) * mm, "end": v(-211.82, 51.37) * mm});
            skLineSegment(sketch, "E808", {"start": v(-211.82, 51.37) * mm, "end": v(-211.37, 48.74) * mm});
            skLineSegment(sketch, "E809", {"start": v(-211.37, 48.74) * mm, "end": v(-211.28, 47.86) * mm});
            skLineSegment(sketch, "E810", {"start": v(-211.28, 47.86) * mm, "end": v(-211.13, 46.33) * mm});
            skLineSegment(sketch, "E811", {"start": v(-211.13, 46.33) * mm, "end": v(-211.17, 41.71) * mm});
            skLineSegment(sketch, "E812", {"start": v(-211.17, 41.71) * mm, "end": v(-212.06, 35.87) * mm});
            skLineSegment(sketch, "E813", {"start": v(-212.06, 35.87) * mm, "end": v(-213.92, 30.4) * mm});
            skLineSegment(sketch, "E814", {"start": v(-213.92, 30.4) * mm, "end": v(-216.7, 25.38) * mm});
            skLineSegment(sketch, "E815", {"start": v(-216.7, 25.38) * mm, "end": v(-220.36, 20.86) * mm});
            skLineSegment(sketch, "E816", {"start": v(-220.36, 20.86) * mm, "end": v(-224.86, 16.9) * mm});
            skLineSegment(sketch, "E817", {"start": v(-224.86, 16.9) * mm, "end": v(-230.14, 13.59) * mm});
            skLineSegment(sketch, "E818", {"start": v(-230.14, 13.59) * mm, "end": v(-234.62, 11.5) * mm});
            skLineSegment(sketch, "E819", {"start": v(-234.62, 11.5) * mm, "end": v(-236.17, 10.96) * mm});
            skLineSegment(sketch, "E820", {"start": v(-236.17, 10.96) * mm, "end": v(-237.13, 10.62) * mm});
            skLineSegment(sketch, "E821", {"start": v(-237.13, 10.62) * mm, "end": v(-236.43, 9.88) * mm});
            skLineSegment(sketch, "E822", {"start": v(-236.43, 9.88) * mm, "end": v(-235.94, 9.37) * mm});
            skLineSegment(sketch, "E823", {"start": v(-235.94, 9.37) * mm, "end": v(-231.97, 4.17) * mm});
            skLineSegment(sketch, "E824", {"start": v(-231.97, 4.17) * mm, "end": v(-231.66, 3.64) * mm});
            skLineSegment(sketch, "E825", {"start": v(-231.66, 3.64) * mm, "end": v(-231.03, 2.56) * mm});
            skLineSegment(sketch, "E826", {"start": v(-231.03, 2.56) * mm, "end": v(-228.86, -0.55) * mm});
            skLineSegment(sketch, "E827", {"start": v(-228.86, -0.55) * mm, "end": v(-225.86, -4.02) * mm});
            skLineSegment(sketch, "E828", {"start": v(-225.86, -4.02) * mm, "end": v(-222.73, -6.82) * mm});
            skLineSegment(sketch, "E829", {"start": v(-222.73, -6.82) * mm, "end": v(-219.59, -9.03) * mm});
            skLineSegment(sketch, "E830", {"start": v(-219.59, -9.03) * mm, "end": v(-216.52, -10.7) * mm});
            skLineSegment(sketch, "E831", {"start": v(-216.52, -10.7) * mm, "end": v(-213.62, -11.94) * mm});
            skLineSegment(sketch, "E832", {"start": v(-213.62, -11.94) * mm, "end": v(-210.98, -12.8) * mm});
            skLineSegment(sketch, "E833", {"start": v(-210.98, -12.8) * mm, "end": v(-209.27, -13.22) * mm});
            skLineSegment(sketch, "E834", {"start": v(-209.27, -13.22) * mm, "end": v(-208.7, -13.33) * mm});
            skLineSegment(sketch, "E835", {"start": v(-208.7, -13.33) * mm, "end": v(-208.44, -13.38) * mm});
            skLineSegment(sketch, "E836", {"start": v(-208.44, -13.38) * mm, "end": v(-207.7, -13.72) * mm});
            skLineSegment(sketch, "E837", {"start": v(-207.7, -13.72) * mm, "end": v(-206.9, -14.42) * mm});
            skLineSegment(sketch, "E838", {"start": v(-206.9, -14.42) * mm, "end": v(-206.37, -15.36) * mm});
            skLineSegment(sketch, "E839", {"start": v(-206.37, -15.36) * mm, "end": v(-206.19, -16.17) * mm});
            skLineSegment(sketch, "E840", {"start": v(-206.19, -16.17) * mm, "end": v(-206.18, -16.44) * mm});
            skLineSegment(sketch, "E841", {"start": v(-206.18, -16.44) * mm, "end": v(-206.17, -26.53) * mm});
            skLineSegment(sketch, "E842", {"start": v(-206.17, -26.53) * mm, "end": v(-206.17, -26.88) * mm});
            skLineSegment(sketch, "E843", {"start": v(-206.17, -26.88) * mm, "end": v(-206.44, -27.95) * mm});
            skLineSegment(sketch, "E844", {"start": v(-206.44, -27.95) * mm, "end": v(-207.06, -28.94) * mm});
            skLineSegment(sketch, "E845", {"start": v(-207.06, -28.94) * mm, "end": v(-207.23, -29.11) * mm});
            skLineSegment(sketch, "E846", {"start": v(-207.23, -29.11) * mm, "end": v(-207.45, -29.33) * mm});
            skLineSegment(sketch, "E847", {"start": v(-207.45, -29.33) * mm, "end": v(-208.83, -30.1) * mm});
            skLineSegment(sketch, "E848", {"start": v(-208.83, -30.1) * mm, "end": v(-210.52, -30.43) * mm});
            skLineSegment(sketch, "E849", {"start": v(-210.52, -30.43) * mm, "end": v(-210.89, -30.43) * mm});
            skLineSegment(sketch, "E850", {"start": v(-210.89, -30.43) * mm, "end": v(-211.75, -30.41) * mm});
            skLineSegment(sketch, "E851", {"start": v(-211.75, -30.41) * mm, "end": v(-214.33, -30.05) * mm});
            skLineSegment(sketch, "E852", {"start": v(-214.33, -30.05) * mm, "end": v(-218.4, -29) * mm});
            skLineSegment(sketch, "E853", {"start": v(-218.4, -29) * mm, "end": v(-222.95, -27.22) * mm});
            skLineSegment(sketch, "E854", {"start": v(-222.95, -27.22) * mm, "end": v(-227.83, -24.64) * mm});
            skLineSegment(sketch, "E855", {"start": v(-227.83, -24.64) * mm, "end": v(-232.88, -21.23) * mm});
            skLineSegment(sketch, "E856", {"start": v(-232.88, -21.23) * mm, "end": v(-237.96, -16.92) * mm});
            skLineSegment(sketch, "E857", {"start": v(-237.96, -16.92) * mm, "end": v(-242.9, -11.65) * mm});
            skLineSegment(sketch, "E858", {"start": v(-242.9, -11.65) * mm, "end": v(-246.5, -7) * mm});
            skLineSegment(sketch, "E859", {"start": v(-246.5, -7) * mm, "end": v(-247.57, -5.38) * mm});
            skLineSegment(sketch, "E860", {"start": v(-247.57, -5.38) * mm, "end": v(-248.4, -4.12) * mm});
            skLineSegment(sketch, "E861", {"start": v(-248.4, -4.12) * mm, "end": v(-251.28, -0.6) * mm});
            skLineSegment(sketch, "E862", {"start": v(-251.28, -0.6) * mm, "end": v(-255.54, 3.36) * mm});
            skLineSegment(sketch, "E863", {"start": v(-255.54, 3.36) * mm, "end": v(-260.33, 6.48) * mm});
            skLineSegment(sketch, "E864", {"start": v(-260.33, 6.48) * mm, "end": v(-264.28, 8.29) * mm});
            skLineSegment(sketch, "E865", {"start": v(-264.28, 8.29) * mm, "end": v(-265.64, 8.74) * mm});
            skLineSegment(sketch, "E866", {"start": v(-252.39, -82.92) * mm, "end": v(-269.3, -82.92) * mm});
            skLineSegment(sketch, "E867", {"start": v(-269.3, -82.92) * mm, "end": v(-269.3, -57.64) * mm});
            skLineSegment(sketch, "E868", {"start": v(-269.3, -57.64) * mm, "end": v(-253.13, -57.64) * mm});
            skLineSegment(sketch, "E869", {"start": v(-253.13, -57.64) * mm, "end": v(-253.13, -62.13) * mm});
            skLineSegment(sketch, "E870", {"start": v(-253.13, -62.13) * mm, "end": v(-264.39, -62.13) * mm});
            skLineSegment(sketch, "E871", {"start": v(-264.39, -62.13) * mm, "end": v(-264.39, -68.18) * mm});
            skLineSegment(sketch, "E872", {"start": v(-264.39, -68.18) * mm, "end": v(-255.38, -68.18) * mm});
            skLineSegment(sketch, "E873", {"start": v(-255.38, -68.18) * mm, "end": v(-255.38, -72.6) * mm});
            skLineSegment(sketch, "E874", {"start": v(-255.38, -72.6) * mm, "end": v(-264.39, -72.6) * mm});
            skLineSegment(sketch, "E875", {"start": v(-264.39, -72.6) * mm, "end": v(-264.39, -78.47) * mm});
            skLineSegment(sketch, "E876", {"start": v(-264.39, -78.47) * mm, "end": v(-252.39, -78.47) * mm});
            skLineSegment(sketch, "E877", {"start": v(-252.39, -78.47) * mm, "end": v(-252.39, -82.92) * mm});
            skLineSegment(sketch, "E878", {"start": v(-278.44, -62.13) * mm, "end": v(-285.45, -62.13) * mm});
            skLineSegment(sketch, "E879", {"start": v(-285.45, -62.13) * mm, "end": v(-285.45, -82.92) * mm});
            skLineSegment(sketch, "E880", {"start": v(-285.45, -82.92) * mm, "end": v(-290.44, -82.92) * mm});
            skLineSegment(sketch, "E881", {"start": v(-290.44, -82.92) * mm, "end": v(-290.44, -62.13) * mm});
            skLineSegment(sketch, "E882", {"start": v(-290.44, -62.13) * mm, "end": v(-297.42, -62.13) * mm});
            skLineSegment(sketch, "E883", {"start": v(-297.42, -62.13) * mm, "end": v(-297.42, -57.64) * mm});
            skLineSegment(sketch, "E884", {"start": v(-297.42, -57.64) * mm, "end": v(-278.44, -57.64) * mm});
            skLineSegment(sketch, "E885", {"start": v(-278.44, -57.64) * mm, "end": v(-278.44, -62.13) * mm});
            skLineSegment(sketch, "E886", {"start": v(-313.86, -83.2) * mm, "end": v(-314.47, -83.2) * mm});
            skLineSegment(sketch, "E887", {"start": v(-314.47, -83.2) * mm, "end": v(-316.3, -82.97) * mm});
            skLineSegment(sketch, "E888", {"start": v(-316.3, -82.97) * mm, "end": v(-318.7, -82.24) * mm});
            skLineSegment(sketch, "E889", {"start": v(-318.7, -82.24) * mm, "end": v(-320.99, -81) * mm});
            skLineSegment(sketch, "E890", {"start": v(-320.99, -81) * mm, "end": v(-322.6, -79.71) * mm});
            skLineSegment(sketch, "E891", {"start": v(-322.6, -79.71) * mm, "end": v(-323.08, -79.22) * mm});
            skLineSegment(sketch, "E892", {"start": v(-323.08, -79.22) * mm, "end": v(-320.09, -75.52) * mm});
            skLineSegment(sketch, "E893", {"start": v(-320.09, -75.52) * mm, "end": v(-319.62, -76.07) * mm});
            skLineSegment(sketch, "E894", {"start": v(-319.62, -76.07) * mm, "end": v(-316.98, -77.93) * mm});
            skLineSegment(sketch, "E895", {"start": v(-316.98, -77.93) * mm, "end": v(-314.58, -78.69) * mm});
            skLineSegment(sketch, "E896", {"start": v(-314.58, -78.69) * mm, "end": v(-313.79, -78.69) * mm});
            skLineSegment(sketch, "E897", {"start": v(-313.79, -78.69) * mm, "end": v(-313.39, -78.69) * mm});
            skLineSegment(sketch, "E898", {"start": v(-313.39, -78.69) * mm, "end": v(-312.2, -78.49) * mm});
            skLineSegment(sketch, "E899", {"start": v(-312.2, -78.49) * mm, "end": v(-311.06, -77.94) * mm});
            skLineSegment(sketch, "E900", {"start": v(-311.06, -77.94) * mm, "end": v(-310.38, -77.1) * mm});
            skLineSegment(sketch, "E901", {"start": v(-310.38, -77.1) * mm, "end": v(-310.15, -76.28) * mm});
            skLineSegment(sketch, "E902", {"start": v(-310.15, -76.28) * mm, "end": v(-310.15, -76.01) * mm});
            skLineSegment(sketch, "E903", {"start": v(-310.15, -76.01) * mm, "end": v(-310.15, -75.72) * mm});
            skLineSegment(sketch, "E904", {"start": v(-310.15, -75.72) * mm, "end": v(-310.41, -74.82) * mm});
            skLineSegment(sketch, "E905", {"start": v(-310.41, -74.82) * mm, "end": v(-311.21, -73.93) * mm});
            skLineSegment(sketch, "E906", {"start": v(-311.21, -73.93) * mm, "end": v(-312.59, -73.19) * mm});
            skLineSegment(sketch, "E907", {"start": v(-312.59, -73.19) * mm, "end": v(-314.07, -72.62) * mm});
            skLineSegment(sketch, "E908", {"start": v(-314.07, -72.62) * mm, "end": v(-314.57, -72.45) * mm});
            skLineSegment(sketch, "E909", {"start": v(-314.57, -72.45) * mm, "end": v(-315.28, -72.2) * mm});
            skLineSegment(sketch, "E910", {"start": v(-315.28, -72.2) * mm, "end": v(-317.37, -71.32) * mm});
            skLineSegment(sketch, "E911", {"start": v(-317.37, -71.32) * mm, "end": v(-319.8, -69.78) * mm});
            skLineSegment(sketch, "E912", {"start": v(-319.8, -69.78) * mm, "end": v(-321.53, -67.6) * mm});
            skLineSegment(sketch, "E913", {"start": v(-321.53, -67.6) * mm, "end": v(-322.19, -65.31) * mm});
            skLineSegment(sketch, "E914", {"start": v(-322.19, -65.31) * mm, "end": v(-322.19, -64.55) * mm});
            skLineSegment(sketch, "E915", {"start": v(-322.19, -64.55) * mm, "end": v(-322.19, -63.84) * mm});
            skLineSegment(sketch, "E916", {"start": v(-322.19, -63.84) * mm, "end": v(-321.56, -61.72) * mm});
            skLineSegment(sketch, "E917", {"start": v(-321.56, -61.72) * mm, "end": v(-319.84, -59.44) * mm});
            skLineSegment(sketch, "E918", {"start": v(-319.84, -59.44) * mm, "end": v(-317.26, -57.91) * mm});
            skLineSegment(sketch, "E919", {"start": v(-317.26, -57.91) * mm, "end": v(-314.87, -57.33) * mm});
            skLineSegment(sketch, "E920", {"start": v(-314.87, -57.33) * mm, "end": v(-314.07, -57.32) * mm});
            skLineSegment(sketch, "E921", {"start": v(-314.07, -57.32) * mm, "end": v(-313.29, -57.31) * mm});
            skLineSegment(sketch, "E922", {"start": v(-313.29, -57.31) * mm, "end": v(-309.56, -58.14) * mm});
            skLineSegment(sketch, "E923", {"start": v(-309.56, -58.14) * mm, "end": v(-306.18, -60) * mm});
            skLineSegment(sketch, "E924", {"start": v(-306.18, -60) * mm, "end": v(-305.56, -60.53) * mm});
            skLineSegment(sketch, "E925", {"start": v(-305.56, -60.53) * mm, "end": v(-308.45, -64.3) * mm});
            skLineSegment(sketch, "E926", {"start": v(-308.45, -64.3) * mm, "end": v(-308.8, -64) * mm});
            skLineSegment(sketch, "E927", {"start": v(-308.8, -64) * mm, "end": v(-309.97, -63.17) * mm});
            skLineSegment(sketch, "E928", {"start": v(-309.97, -63.17) * mm, "end": v(-311.4, -62.4) * mm});
            skLineSegment(sketch, "E929", {"start": v(-311.4, -62.4) * mm, "end": v(-312.74, -61.95) * mm});
            skLineSegment(sketch, "E930", {"start": v(-312.74, -61.95) * mm, "end": v(-313.66, -61.8) * mm});
            skLineSegment(sketch, "E931", {"start": v(-313.66, -61.8) * mm, "end": v(-313.96, -61.8) * mm});
            skLineSegment(sketch, "E932", {"start": v(-313.96, -61.8) * mm, "end": v(-314.27, -61.8) * mm});
            skLineSegment(sketch, "E933", {"start": v(-314.27, -61.8) * mm, "end": v(-315.17, -61.98) * mm});
            skLineSegment(sketch, "E934", {"start": v(-315.17, -61.98) * mm, "end": v(-316.13, -62.47) * mm});
            skLineSegment(sketch, "E935", {"start": v(-316.13, -62.47) * mm, "end": v(-316.76, -63.26) * mm});
            skLineSegment(sketch, "E936", {"start": v(-316.76, -63.26) * mm, "end": v(-316.99, -64.07) * mm});
            skLineSegment(sketch, "E937", {"start": v(-316.99, -64.07) * mm, "end": v(-316.99, -64.33) * mm});
            skLineSegment(sketch, "E938", {"start": v(-316.99, -64.33) * mm, "end": v(-317, -64.59) * mm});
            skLineSegment(sketch, "E939", {"start": v(-317, -64.59) * mm, "end": v(-316.75, -65.36) * mm});
            skLineSegment(sketch, "E940", {"start": v(-316.75, -65.36) * mm, "end": v(-315.97, -66.19) * mm});
            skLineSegment(sketch, "E941", {"start": v(-315.97, -66.19) * mm, "end": v(-314.64, -66.93) * mm});
            skLineSegment(sketch, "E942", {"start": v(-314.64, -66.93) * mm, "end": v(-313.23, -67.53) * mm});
            skLineSegment(sketch, "E943", {"start": v(-313.23, -67.53) * mm, "end": v(-312.75, -67.72) * mm});
            skLineSegment(sketch, "E944", {"start": v(-312.75, -67.72) * mm, "end": v(-311.98, -68.02) * mm});
            skLineSegment(sketch, "E945", {"start": v(-311.98, -68.02) * mm, "end": v(-309.68, -68.96) * mm});
            skLineSegment(sketch, "E946", {"start": v(-309.68, -68.96) * mm, "end": v(-307.2, -70.4) * mm});
            skLineSegment(sketch, "E947", {"start": v(-307.2, -70.4) * mm, "end": v(-305.53, -72.42) * mm});
            skLineSegment(sketch, "E948", {"start": v(-305.53, -72.42) * mm, "end": v(-304.92, -74.69) * mm});
            skLineSegment(sketch, "E949", {"start": v(-304.92, -74.69) * mm, "end": v(-304.92, -75.44) * mm});
            skLineSegment(sketch, "E950", {"start": v(-304.92, -75.44) * mm, "end": v(-304.92, -75.92) * mm});
            skLineSegment(sketch, "E951", {"start": v(-304.92, -75.92) * mm, "end": v(-305.13, -77.36) * mm});
            skLineSegment(sketch, "E952", {"start": v(-305.13, -77.36) * mm, "end": v(-305.74, -78.99) * mm});
            skLineSegment(sketch, "E953", {"start": v(-305.74, -78.99) * mm, "end": v(-306.66, -80.33) * mm});
            skLineSegment(sketch, "E954", {"start": v(-306.66, -80.33) * mm, "end": v(-307.84, -81.4) * mm});
            skLineSegment(sketch, "E955", {"start": v(-307.84, -81.4) * mm, "end": v(-309.22, -82.2) * mm});
            skLineSegment(sketch, "E956", {"start": v(-309.22, -82.2) * mm, "end": v(-310.72, -82.77) * mm});
            skLineSegment(sketch, "E957", {"start": v(-310.72, -82.77) * mm, "end": v(-312.29, -83.1) * mm});
            skLineSegment(sketch, "E958", {"start": v(-312.29, -83.1) * mm, "end": v(-313.46, -83.2) * mm});
            skLineSegment(sketch, "E959", {"start": v(-313.46, -83.2) * mm, "end": v(-313.86, -83.2) * mm});
            skLineSegment(sketch, "E960", {"start": v(-59.35, 81.32) * mm, "end": v(-59.33, 81.37) * mm});
            skLineSegment(sketch, "E961", {"start": v(-59.33, 81.37) * mm, "end": v(-58.93, 81.6) * mm});
            skLineSegment(sketch, "E962", {"start": v(-58.93, 81.6) * mm, "end": v(-58.8, 81.6) * mm});
            skLineSegment(sketch, "E963", {"start": v(-58.8, 81.6) * mm, "end": v(-34.9, 81.6) * mm});
            skLineSegment(sketch, "E964", {"start": v(-34.9, 81.6) * mm, "end": v(38.22, -1.58) * mm});
            skLineSegment(sketch, "E965", {"start": v(38.22, -1.58) * mm, "end": v(38.35, -1.74) * mm});
            skLineSegment(sketch, "E966", {"start": v(38.35, -1.74) * mm, "end": v(39.24, -2.2) * mm});
            skLineSegment(sketch, "E967", {"start": v(39.24, -2.2) * mm, "end": v(40.23, -2.18) * mm});
            skLineSegment(sketch, "E968", {"start": v(40.23, -2.18) * mm, "end": v(40.42, -2.1) * mm});
            skLineSegment(sketch, "E969", {"start": v(40.42, -2.1) * mm, "end": v(40.62, -2.03) * mm});
            skLineSegment(sketch, "E970", {"start": v(40.62, -2.03) * mm, "end": v(41.36, -1.37) * mm});
            skLineSegment(sketch, "E971", {"start": v(41.36, -1.37) * mm, "end": v(41.71, -0.52) * mm});
            skLineSegment(sketch, "E972", {"start": v(41.71, -0.52) * mm, "end": v(41.71, -0.24) * mm});
            skLineSegment(sketch, "E973", {"start": v(41.71, -0.24) * mm, "end": v(41.71, 80.92) * mm});
            skLineSegment(sketch, "E974", {"start": v(41.71, 80.92) * mm, "end": v(41.71, 81.04) * mm});
            skLineSegment(sketch, "E975", {"start": v(41.71, 81.04) * mm, "end": v(41.91, 81.4) * mm});
            skLineSegment(sketch, "E976", {"start": v(41.91, 81.4) * mm, "end": v(42.27, 81.6) * mm});
            skLineSegment(sketch, "E977", {"start": v(42.27, 81.6) * mm, "end": v(42.4, 81.6) * mm});
            skLineSegment(sketch, "E978", {"start": v(42.4, 81.6) * mm, "end": v(66.38, 81.6) * mm});
            skLineSegment(sketch, "E979", {"start": v(66.38, 81.6) * mm, "end": v(66.52, 81.6) * mm});
            skLineSegment(sketch, "E980", {"start": v(66.52, 81.6) * mm, "end": v(66.9, 81.37) * mm});
            skLineSegment(sketch, "E981", {"start": v(66.9, 81.37) * mm, "end": v(66.93, 81.32) * mm});
            skLineSegment(sketch, "E982", {"start": v(66.93, 81.32) * mm, "end": v(66.97, 81.27) * mm});
            skLineSegment(sketch, "E983", {"start": v(66.97, 81.27) * mm, "end": v(67.04, 80.76) * mm});
            skLineSegment(sketch, "E984", {"start": v(67.04, 80.76) * mm, "end": v(67.03, 80.7) * mm});
            skLineSegment(sketch, "E985", {"start": v(67.03, 80.7) * mm, "end": v(61.67, 64.64) * mm});
            skLineSegment(sketch, "E986", {"start": v(61.67, 64.64) * mm, "end": v(58.67, 64.64) * mm});
            skLineSegment(sketch, "E987", {"start": v(58.67, 64.64) * mm, "end": v(58.67, -29.1) * mm});
            skLineSegment(sketch, "E988", {"start": v(58.67, -29.1) * mm, "end": v(58.67, -29.25) * mm});
            skLineSegment(sketch, "E989", {"start": v(58.67, -29.25) * mm, "end": v(58.55, -29.68) * mm});
            skLineSegment(sketch, "E990", {"start": v(58.55, -29.68) * mm, "end": v(58.24, -30.15) * mm});
            skLineSegment(sketch, "E991", {"start": v(58.24, -30.15) * mm, "end": v(57.77, -30.46) * mm});
            skLineSegment(sketch, "E992", {"start": v(57.77, -30.46) * mm, "end": v(57.34, -30.58) * mm});
            skLineSegment(sketch, "E993", {"start": v(57.34, -30.58) * mm, "end": v(57.2, -30.58) * mm});
            skLineSegment(sketch, "E994", {"start": v(57.2, -30.58) * mm, "end": v(42, -30.58) * mm});
            skLineSegment(sketch, "E995", {"start": v(42, -30.58) * mm, "end": v(41.84, -30.58) * mm});
            skLineSegment(sketch, "E996", {"start": v(41.84, -30.58) * mm, "end": v(41.4, -30.45) * mm});
            skLineSegment(sketch, "E997", {"start": v(41.4, -30.45) * mm, "end": v(40.97, -30.17) * mm});
            skLineSegment(sketch, "E998", {"start": v(40.97, -30.17) * mm, "end": v(40.9, -30.1) * mm});
            skLineSegment(sketch, "E999", {"start": v(40.9, -30.1) * mm, "end": v(-30.64, 51.29) * mm});
            skLineSegment(sketch, "E1000", {"start": v(-30.64, 51.29) * mm, "end": v(-30.78, 51.44) * mm});
            skLineSegment(sketch, "E1001", {"start": v(-30.78, 51.44) * mm, "end": v(-31.66, 51.9) * mm});
            skLineSegment(sketch, "E1002", {"start": v(-31.66, 51.9) * mm, "end": v(-32.65, 51.89) * mm});
            skLineSegment(sketch, "E1003", {"start": v(-32.65, 51.89) * mm, "end": v(-32.84, 51.8) * mm});
            skLineSegment(sketch, "E1004", {"start": v(-32.84, 51.8) * mm, "end": v(-33.04, 51.74) * mm});
            skLineSegment(sketch, "E1005", {"start": v(-33.04, 51.74) * mm, "end": v(-33.78, 51.08) * mm});
            skLineSegment(sketch, "E1006", {"start": v(-33.78, 51.08) * mm, "end": v(-34.13, 50.22) * mm});
            skLineSegment(sketch, "E1007", {"start": v(-34.13, 50.22) * mm, "end": v(-34.13, 49.94) * mm});
            skLineSegment(sketch, "E1008", {"start": v(-34.13, 49.94) * mm, "end": v(-34.13, -29.9) * mm});
            skLineSegment(sketch, "E1009", {"start": v(-34.13, -29.9) * mm, "end": v(-34.13, -30.02) * mm});
            skLineSegment(sketch, "E1010", {"start": v(-34.13, -30.02) * mm, "end": v(-34.34, -30.38) * mm});
            skLineSegment(sketch, "E1011", {"start": v(-34.34, -30.38) * mm, "end": v(-34.7, -30.58) * mm});
            skLineSegment(sketch, "E1012", {"start": v(-34.7, -30.58) * mm, "end": v(-34.82, -30.58) * mm});
            skLineSegment(sketch, "E1013", {"start": v(-34.82, -30.58) * mm, "end": v(-58.41, -30.58) * mm});
            skLineSegment(sketch, "E1014", {"start": v(-58.41, -30.58) * mm, "end": v(-58.52, -30.58) * mm});
            skLineSegment(sketch, "E1015", {"start": v(-58.52, -30.58) * mm, "end": v(-58.85, -30.47) * mm});
            skLineSegment(sketch, "E1016", {"start": v(-58.85, -30.47) * mm, "end": v(-59.15, -30.24) * mm});
            skLineSegment(sketch, "E1017", {"start": v(-59.15, -30.24) * mm, "end": v(-59.2, -30.18) * mm});
            skLineSegment(sketch, "E1018", {"start": v(-59.2, -30.18) * mm, "end": v(-59.24, -30.12) * mm});
            skLineSegment(sketch, "E1019", {"start": v(-59.24, -30.12) * mm, "end": v(-59.35, -29.39) * mm});
            skLineSegment(sketch, "E1020", {"start": v(-59.35, -29.39) * mm, "end": v(-59.33, -29.31) * mm});
            skLineSegment(sketch, "E1021", {"start": v(-59.33, -29.31) * mm, "end": v(-54.1, -13.62) * mm});
            skLineSegment(sketch, "E1022", {"start": v(-54.1, -13.62) * mm, "end": v(-51.1, -13.62) * mm});
            skLineSegment(sketch, "E1023", {"start": v(-51.1, -13.62) * mm, "end": v(-51.1, 64.64) * mm});
            skLineSegment(sketch, "E1024", {"start": v(-51.1, 64.64) * mm, "end": v(-54.1, 64.64) * mm});
            skLineSegment(sketch, "E1025", {"start": v(-54.1, 64.64) * mm, "end": v(-59.45, 80.7) * mm});
            skLineSegment(sketch, "E1026", {"start": v(-59.45, 80.7) * mm, "end": v(-59.47, 80.76) * mm});
            skLineSegment(sketch, "E1027", {"start": v(-59.47, 80.76) * mm, "end": v(-59.39, 81.27) * mm});
            skLineSegment(sketch, "E1028", {"start": v(-59.39, 81.27) * mm, "end": v(-59.35, 81.32) * mm});
            skLineSegment(sketch, "E1029", {"start": v(-431.4, -284.92) * mm, "end": v(431.4, -284.92) * mm});
            skLineSegment(sketch, "E1030", {"start": v(431.4, -284.92) * mm, "end": v(431.4, 284.92) * mm});
            skLineSegment(sketch, "E1031", {"start": v(431.4, 284.92) * mm, "end": v(-431.4, 284.92) * mm});
            skLineSegment(sketch, "E1032", {"start": v(-431.4, 284.92) * mm, "end": v(-431.4, -284.92) * mm});
            skLineSegment(sketch, "E1033", {"start": v(-232.95, -63.66) * mm, "end": v(-236.3, -73.6) * mm});
            skLineSegment(sketch, "E1034", {"start": v(-236.3, -73.6) * mm, "end": v(-229.5, -73.6) * mm});
            skLineSegment(sketch, "E1035", {"start": v(-229.5, -73.6) * mm, "end": v(-232.88, -63.66) * mm});
            skLineSegment(sketch, "E1036", {"start": v(-232.88, -63.66) * mm, "end": v(-232.95, -63.66) * mm});
            skLineSegment(sketch, "E1037", {"start": v(-28.03, -63.66) * mm, "end": v(-31.38, -73.6) * mm});
            skLineSegment(sketch, "E1038", {"start": v(-31.38, -73.6) * mm, "end": v(-24.58, -73.6) * mm});
            skLineSegment(sketch, "E1039", {"start": v(-24.58, -73.6) * mm, "end": v(-27.96, -63.66) * mm});
            skLineSegment(sketch, "E1040", {"start": v(-27.96, -63.66) * mm, "end": v(-28.03, -63.66) * mm});
            skLineSegment(sketch, "E1041", {"start": v(29.73, -62.02) * mm, "end": v(28.95, -62.02) * mm});
            skLineSegment(sketch, "E1042", {"start": v(28.95, -62.02) * mm, "end": v(26.6, -62.67) * mm});
            skLineSegment(sketch, "E1043", {"start": v(26.6, -62.67) * mm, "end": v(24.16, -64.43) * mm});
            skLineSegment(sketch, "E1044", {"start": v(24.16, -64.43) * mm, "end": v(22.57, -67.05) * mm});
            skLineSegment(sketch, "E1045", {"start": v(22.57, -67.05) * mm, "end": v(22, -69.48) * mm});
            skLineSegment(sketch, "E1046", {"start": v(22, -69.48) * mm, "end": v(22, -70.28) * mm});
            skLineSegment(sketch, "E1047", {"start": v(22, -70.28) * mm, "end": v(22, -71.1) * mm});
            skLineSegment(sketch, "E1048", {"start": v(22, -71.1) * mm, "end": v(22.57, -73.51) * mm});
            skLineSegment(sketch, "E1049", {"start": v(22.57, -73.51) * mm, "end": v(24.16, -76.14) * mm});
            skLineSegment(sketch, "E1050", {"start": v(24.16, -76.14) * mm, "end": v(26.6, -77.9) * mm});
            skLineSegment(sketch, "E1051", {"start": v(26.6, -77.9) * mm, "end": v(28.95, -78.54) * mm});
            skLineSegment(sketch, "E1052", {"start": v(28.95, -78.54) * mm, "end": v(29.73, -78.54) * mm});
            skLineSegment(sketch, "E1053", {"start": v(29.73, -78.54) * mm, "end": v(30.49, -78.54) * mm});
            skLineSegment(sketch, "E1054", {"start": v(30.49, -78.54) * mm, "end": v(32.76, -77.92) * mm});
            skLineSegment(sketch, "E1055", {"start": v(32.76, -77.92) * mm, "end": v(35.17, -76.19) * mm});
            skLineSegment(sketch, "E1056", {"start": v(35.17, -76.19) * mm, "end": v(36.77, -73.57) * mm});
            skLineSegment(sketch, "E1057", {"start": v(36.77, -73.57) * mm, "end": v(37.35, -71.1) * mm});
            skLineSegment(sketch, "E1058", {"start": v(37.35, -71.1) * mm, "end": v(37.35, -70.28) * mm});
            skLineSegment(sketch, "E1059", {"start": v(37.35, -70.28) * mm, "end": v(37.35, -69.46) * mm});
            skLineSegment(sketch, "E1060", {"start": v(37.35, -69.46) * mm, "end": v(36.77, -66.98) * mm});
            skLineSegment(sketch, "E1061", {"start": v(36.77, -66.98) * mm, "end": v(35.17, -64.36) * mm});
            skLineSegment(sketch, "E1062", {"start": v(35.17, -64.36) * mm, "end": v(32.76, -62.64) * mm});
            skLineSegment(sketch, "E1063", {"start": v(32.76, -62.64) * mm, "end": v(30.49, -62.02) * mm});
            skLineSegment(sketch, "E1064", {"start": v(30.49, -62.02) * mm, "end": v(29.73, -62.02) * mm});
            skLineSegment(sketch, "E1065", {"start": v(64.3, -62.02) * mm, "end": v(63.51, -62.02) * mm});
            skLineSegment(sketch, "E1066", {"start": v(63.51, -62.02) * mm, "end": v(61.16, -62.67) * mm});
            skLineSegment(sketch, "E1067", {"start": v(61.16, -62.67) * mm, "end": v(58.72, -64.43) * mm});
            skLineSegment(sketch, "E1068", {"start": v(58.72, -64.43) * mm, "end": v(57.13, -67.05) * mm});
            skLineSegment(sketch, "E1069", {"start": v(57.13, -67.05) * mm, "end": v(56.57, -69.48) * mm});
            skLineSegment(sketch, "E1070", {"start": v(56.57, -69.48) * mm, "end": v(56.57, -70.28) * mm});
            skLineSegment(sketch, "E1071", {"start": v(56.57, -70.28) * mm, "end": v(56.57, -71.1) * mm});
            skLineSegment(sketch, "E1072", {"start": v(56.57, -71.1) * mm, "end": v(57.13, -73.51) * mm});
            skLineSegment(sketch, "E1073", {"start": v(57.13, -73.51) * mm, "end": v(58.72, -76.14) * mm});
            skLineSegment(sketch, "E1074", {"start": v(58.72, -76.14) * mm, "end": v(61.16, -77.9) * mm});
            skLineSegment(sketch, "E1075", {"start": v(61.16, -77.9) * mm, "end": v(63.51, -78.54) * mm});
            skLineSegment(sketch, "E1076", {"start": v(63.51, -78.54) * mm, "end": v(64.3, -78.54) * mm});
            skLineSegment(sketch, "E1077", {"start": v(64.3, -78.54) * mm, "end": v(65.05, -78.54) * mm});
            skLineSegment(sketch, "E1078", {"start": v(65.05, -78.54) * mm, "end": v(67.32, -77.92) * mm});
            skLineSegment(sketch, "E1079", {"start": v(67.32, -77.92) * mm, "end": v(69.73, -76.19) * mm});
            skLineSegment(sketch, "E1080", {"start": v(69.73, -76.19) * mm, "end": v(71.33, -73.57) * mm});
            skLineSegment(sketch, "E1081", {"start": v(71.33, -73.57) * mm, "end": v(71.92, -71.1) * mm});
            skLineSegment(sketch, "E1082", {"start": v(71.92, -71.1) * mm, "end": v(71.92, -70.28) * mm});
            skLineSegment(sketch, "E1083", {"start": v(71.92, -70.28) * mm, "end": v(71.92, -69.46) * mm});
            skLineSegment(sketch, "E1084", {"start": v(71.92, -69.46) * mm, "end": v(71.33, -66.98) * mm});
            skLineSegment(sketch, "E1085", {"start": v(71.33, -66.98) * mm, "end": v(69.73, -64.36) * mm});
            skLineSegment(sketch, "E1086", {"start": v(69.73, -64.36) * mm, "end": v(67.32, -62.64) * mm});
            skLineSegment(sketch, "E1087", {"start": v(67.32, -62.64) * mm, "end": v(65.05, -62.02) * mm});
            skLineSegment(sketch, "E1088", {"start": v(65.05, -62.02) * mm, "end": v(64.3, -62.02) * mm});
            skLineSegment(sketch, "E1089", {"start": v(-131.32, 64.64) * mm, "end": v(-131.9, 64.64) * mm});
            skLineSegment(sketch, "E1090", {"start": v(-131.9, 64.64) * mm, "end": v(-137.5, 50.23) * mm});
            skLineSegment(sketch, "E1091", {"start": v(-137.5, 50.23) * mm, "end": v(-150.72, 16.2) * mm});
            skLineSegment(sketch, "E1092", {"start": v(-150.72, 16.2) * mm, "end": v(-112.5, 16.2) * mm});
            skLineSegment(sketch, "E1093", {"start": v(-112.5, 16.2) * mm, "end": v(-125.72, 50.23) * mm});
            skLineSegment(sketch, "E1094", {"start": v(-125.72, 50.23) * mm, "end": v(-131.32, 64.64) * mm});
            skLineSegment(sketch, "E1095", {"start": v(-231.94, 32.93) * mm, "end": v(-231.32, 33.68) * mm});
            skLineSegment(sketch, "E1096", {"start": v(-231.32, 33.68) * mm, "end": v(-229.8, 36.22) * mm});
            skLineSegment(sketch, "E1097", {"start": v(-229.8, 36.22) * mm, "end": v(-228.5, 39.87) * mm});
            skLineSegment(sketch, "E1098", {"start": v(-228.5, 39.87) * mm, "end": v(-228.04, 43.82) * mm});
            skLineSegment(sketch, "E1099", {"start": v(-228.04, 43.82) * mm, "end": v(-228.24, 47) * mm});
            skLineSegment(sketch, "E1100", {"start": v(-228.24, 47) * mm, "end": v(-228.43, 48.04) * mm});
            skLineSegment(sketch, "E1101", {"start": v(-228.43, 48.04) * mm, "end": v(-228.6, 48.93) * mm});
            skLineSegment(sketch, "E1102", {"start": v(-228.6, 48.93) * mm, "end": v(-229.45, 51.55) * mm});
            skLineSegment(sketch, "E1103", {"start": v(-229.45, 51.55) * mm, "end": v(-231.07, 54.75) * mm});
            skLineSegment(sketch, "E1104", {"start": v(-231.07, 54.75) * mm, "end": v(-233.23, 57.6) * mm});
            skLineSegment(sketch, "E1105", {"start": v(-233.23, 57.6) * mm, "end": v(-235.85, 60.06) * mm});
            skLineSegment(sketch, "E1106", {"start": v(-235.85, 60.06) * mm, "end": v(-238.88, 62.05) * mm});
            skLineSegment(sketch, "E1107", {"start": v(-238.88, 62.05) * mm, "end": v(-242.25, 63.54) * mm});
            skLineSegment(sketch, "E1108", {"start": v(-242.25, 63.54) * mm, "end": v(-245.9, 64.47) * mm});
            skLineSegment(sketch, "E1109", {"start": v(-245.9, 64.47) * mm, "end": v(-248.79, 64.8) * mm});
            skLineSegment(sketch, "E1110", {"start": v(-248.79, 64.8) * mm, "end": v(-249.75, 64.8) * mm});
            skLineSegment(sketch, "E1111", {"start": v(-249.75, 64.8) * mm, "end": v(-294.8, 64.8) * mm});
            skLineSegment(sketch, "E1112", {"start": v(-294.8, 64.8) * mm, "end": v(-295.12, 64.8) * mm});
            skLineSegment(sketch, "E1113", {"start": v(-295.12, 64.8) * mm, "end": v(-296.06, 64.54) * mm});
            skLineSegment(sketch, "E1114", {"start": v(-296.06, 64.54) * mm, "end": v(-297.09, 63.85) * mm});
            skLineSegment(sketch, "E1115", {"start": v(-297.09, 63.85) * mm, "end": v(-297.78, 62.83) * mm});
            skLineSegment(sketch, "E1116", {"start": v(-297.78, 62.83) * mm, "end": v(-298.03, 61.89) * mm});
            skLineSegment(sketch, "E1117", {"start": v(-298.03, 61.89) * mm, "end": v(-298.03, 61.57) * mm});
            skLineSegment(sketch, "E1118", {"start": v(-298.03, 61.57) * mm, "end": v(-298.03, 28.9) * mm});
            skLineSegment(sketch, "E1119", {"start": v(-298.03, 28.9) * mm, "end": v(-298.03, 28.59) * mm});
            skLineSegment(sketch, "E1120", {"start": v(-298.03, 28.59) * mm, "end": v(-297.78, 27.65) * mm});
            skLineSegment(sketch, "E1121", {"start": v(-297.78, 27.65) * mm, "end": v(-297.09, 26.62) * mm});
            skLineSegment(sketch, "E1122", {"start": v(-297.09, 26.62) * mm, "end": v(-296.06, 25.93) * mm});
            skLineSegment(sketch, "E1123", {"start": v(-296.06, 25.93) * mm, "end": v(-295.12, 25.68) * mm});
            skLineSegment(sketch, "E1124", {"start": v(-295.12, 25.68) * mm, "end": v(-294.8, 25.68) * mm});
            skLineSegment(sketch, "E1125", {"start": v(-294.8, 25.68) * mm, "end": v(-248.89, 25.68) * mm});
            skLineSegment(sketch, "E1126", {"start": v(-248.89, 25.68) * mm, "end": v(-247.63, 25.68) * mm});
            skLineSegment(sketch, "E1127", {"start": v(-247.63, 25.68) * mm, "end": v(-243.84, 26.17) * mm});
            skLineSegment(sketch, "E1128", {"start": v(-243.84, 26.17) * mm, "end": v(-239.24, 27.58) * mm});
            skLineSegment(sketch, "E1129", {"start": v(-239.24, 27.58) * mm, "end": v(-235.22, 29.86) * mm});
            skLineSegment(sketch, "E1130", {"start": v(-235.22, 29.86) * mm, "end": v(-232.65, 32.07) * mm});
            skLineSegment(sketch, "E1131", {"start": v(-232.65, 32.07) * mm, "end": v(-231.94, 32.93) * mm});
            skLineSegment(sketch, "E1132", {"start": v(310.04, -62.13) * mm, "end": v(306.52, -62.13) * mm});
            skLineSegment(sketch, "E1133", {"start": v(306.52, -62.13) * mm, "end": v(306.52, -78.47) * mm});
            skLineSegment(sketch, "E1134", {"start": v(306.52, -78.47) * mm, "end": v(309.73, -78.47) * mm});
            skLineSegment(sketch, "E1135", {"start": v(309.73, -78.47) * mm, "end": v(310.56, -78.47) * mm});
            skLineSegment(sketch, "E1136", {"start": v(310.56, -78.47) * mm, "end": v(313.07, -77.85) * mm});
            skLineSegment(sketch, "E1137", {"start": v(313.07, -77.85) * mm, "end": v(315.65, -76.13) * mm});
            skLineSegment(sketch, "E1138", {"start": v(315.65, -76.13) * mm, "end": v(317.3, -73.54) * mm});
            skLineSegment(sketch, "E1139", {"start": v(317.3, -73.54) * mm, "end": v(317.88, -71.12) * mm});
            skLineSegment(sketch, "E1140", {"start": v(317.88, -71.12) * mm, "end": v(317.88, -70.32) * mm});
            skLineSegment(sketch, "E1141", {"start": v(317.88, -70.32) * mm, "end": v(317.88, -69.5) * mm});
            skLineSegment(sketch, "E1142", {"start": v(317.88, -69.5) * mm, "end": v(317.3, -67.04) * mm});
            skLineSegment(sketch, "E1143", {"start": v(317.3, -67.04) * mm, "end": v(315.67, -64.45) * mm});
            skLineSegment(sketch, "E1144", {"start": v(315.67, -64.45) * mm, "end": v(313.2, -62.74) * mm});
            skLineSegment(sketch, "E1145", {"start": v(313.2, -62.74) * mm, "end": v(310.83, -62.13) * mm});
            skLineSegment(sketch, "E1146", {"start": v(310.83, -62.13) * mm, "end": v(310.04, -62.13) * mm});
            skLineSegment(sketch, "E1147", {"start": v(95.44, -62.13) * mm, "end": v(91.91, -62.13) * mm});
            skLineSegment(sketch, "E1148", {"start": v(91.91, -62.13) * mm, "end": v(91.91, -78.47) * mm});
            skLineSegment(sketch, "E1149", {"start": v(91.91, -78.47) * mm, "end": v(95.12, -78.47) * mm});
            skLineSegment(sketch, "E1150", {"start": v(95.12, -78.47) * mm, "end": v(95.95, -78.47) * mm});
            skLineSegment(sketch, "E1151", {"start": v(95.95, -78.47) * mm, "end": v(98.46, -77.85) * mm});
            skLineSegment(sketch, "E1152", {"start": v(98.46, -77.85) * mm, "end": v(101.04, -76.13) * mm});
            skLineSegment(sketch, "E1153", {"start": v(101.04, -76.13) * mm, "end": v(102.69, -73.54) * mm});
            skLineSegment(sketch, "E1154", {"start": v(102.69, -73.54) * mm, "end": v(103.27, -71.12) * mm});
            skLineSegment(sketch, "E1155", {"start": v(103.27, -71.12) * mm, "end": v(103.27, -70.32) * mm});
            skLineSegment(sketch, "E1156", {"start": v(103.27, -70.32) * mm, "end": v(103.27, -69.5) * mm});
            skLineSegment(sketch, "E1157", {"start": v(103.27, -69.5) * mm, "end": v(102.69, -67.04) * mm});
            skLineSegment(sketch, "E1158", {"start": v(102.69, -67.04) * mm, "end": v(101.06, -64.45) * mm});
            skLineSegment(sketch, "E1159", {"start": v(101.06, -64.45) * mm, "end": v(98.58, -62.74) * mm});
            skLineSegment(sketch, "E1160", {"start": v(98.58, -62.74) * mm, "end": v(96.22, -62.13) * mm});
            skLineSegment(sketch, "E1161", {"start": v(96.22, -62.13) * mm, "end": v(95.44, -62.13) * mm});
            skSolve(sketch);
        }
        {
            var Q0;
            Q0=makeQuery(id+"F0.imprint","IMPRINT",FACE,{"disambiguationData":[TD([[makeQuery(id+"F0.imprint","IMPRINT",EDGE,{"derivedFrom":sQuery(id+"F0.wireOp",EDGE,"E0")}),1.0]])]});
            var Q1;
            Q1=makeQuery(id+"F0.imprint","IMPRINT",FACE,{"disambiguationData":[TD([[makeQuery(id+"F0.imprint","IMPRINT",EDGE,{"derivedFrom":sQuery(id+"F0.wireOp",EDGE,"E1095")}),1.0]])]});
            var Q2;
            Q2=makeQuery(id+"F0.imprint","IMPRINT",FACE,{"disambiguationData":[TD([[makeQuery(id+"F0.imprint","IMPRINT",EDGE,{"derivedFrom":sQuery(id+"F0.wireOp",EDGE,"E1089")}),1.0]])]});
            var Q3;
            Q3=makeQuery(id+"F0.imprint","IMPRINT",FACE,{"disambiguationData":[TD([[makeQuery(id+"F0.imprint","IMPRINT",EDGE,{"derivedFrom":sQuery(id+"F0.wireOp",EDGE,"E1132")}),1.0]])]});
            var Q4;
            Q4=makeQuery(id+"F0.imprint","IMPRINT",FACE,{"disambiguationData":[TD([[makeQuery(id+"F0.imprint","IMPRINT",EDGE,{"derivedFrom":sQuery(id+"F0.wireOp",EDGE,"E1147")}),1.0]])]});
            var Q5;
            Q5=makeQuery(id+"F0.imprint","IMPRINT",FACE,{"disambiguationData":[TD([[makeQuery(id+"F0.imprint","IMPRINT",EDGE,{"derivedFrom":sQuery(id+"F0.wireOp",EDGE,"E1065")}),1.0]])]});
            var Q6;
            Q6=makeQuery(id+"F0.imprint","IMPRINT",FACE,{"disambiguationData":[TD([[makeQuery(id+"F0.imprint","IMPRINT",EDGE,{"derivedFrom":sQuery(id+"F0.wireOp",EDGE,"E1037")}),1.0]])]});
            var Q7;
            Q7=makeQuery(id+"F0.imprint","IMPRINT",FACE,{"disambiguationData":[TD([[makeQuery(id+"F0.imprint","IMPRINT",EDGE,{"derivedFrom":sQuery(id+"F0.wireOp",EDGE,"E1033")}),1.0]])]});
            var Q8;
            Q8=makeQuery(id+"F0.imprint","IMPRINT",FACE,{"disambiguationData":[TD([[makeQuery(id+"F0.imprint","IMPRINT",EDGE,{"derivedFrom":sQuery(id+"F0.wireOp",EDGE,"E1041")}),1.0]])]});
            extrude(context, id + "F1", {"entities" : qUnion([Q0, Q1, Q2, Q3, Q4, Q5, Q6, Q7, Q8]), "depth" : 0.25 * mm, "offsetDistance" : 25.4 * mm});
        }
        {
            var Q0;
            Q0=makeQuery(id+"F0.imprint","IMPRINT",FACE,{"disambiguationData":[TD([[makeQuery(id+"F0.imprint","IMPRINT",EDGE,{"derivedFrom":sQuery(id+"F0.wireOp",EDGE,"E326")}),-1.0]])]});
            var Q1;
            Q1=makeQuery(id+"F0.imprint","IMPRINT",FACE,{"disambiguationData":[TD([[makeQuery(id+"F0.imprint","IMPRINT",EDGE,{"derivedFrom":sQuery(id+"F0.wireOp",EDGE,"E346")}),-1.0]])]});
            var Q2;
            Q2=makeQuery(id+"F0.imprint","IMPRINT",FACE,{"disambiguationData":[TD([[makeQuery(id+"F0.imprint","IMPRINT",EDGE,{"derivedFrom":sQuery(id+"F0.wireOp",EDGE,"E382")}),-1.0]])]});
            var Q3;
            Q3=makeQuery(id+"F0.imprint","IMPRINT",FACE,{"disambiguationData":[TD([[makeQuery(id+"F0.imprint","IMPRINT",EDGE,{"derivedFrom":sQuery(id+"F0.wireOp",EDGE,"E657")}),-1.0]])]});
            var Q4;
            Q4=makeQuery(id+"F0.imprint","IMPRINT",FACE,{"disambiguationData":[TD([[makeQuery(id+"F0.imprint","IMPRINT",EDGE,{"derivedFrom":sQuery(id+"F0.wireOp",EDGE,"E677")}),-1.0]])]});
            var Q5;
            Q5=makeQuery(id+"F0.imprint","IMPRINT",FACE,{"disambiguationData":[TD([[makeQuery(id+"F0.imprint","IMPRINT",EDGE,{"derivedFrom":sQuery(id+"F0.wireOp",EDGE,"E713")}),-1.0]])]});
            extrude(context, id + "F2", {"entities" : qUnion([Q0, Q1, Q2, Q3, Q4, Q5]), "depth" : 0.25 * mm, "offsetDistance" : 25.4 * mm});
        }
    });
